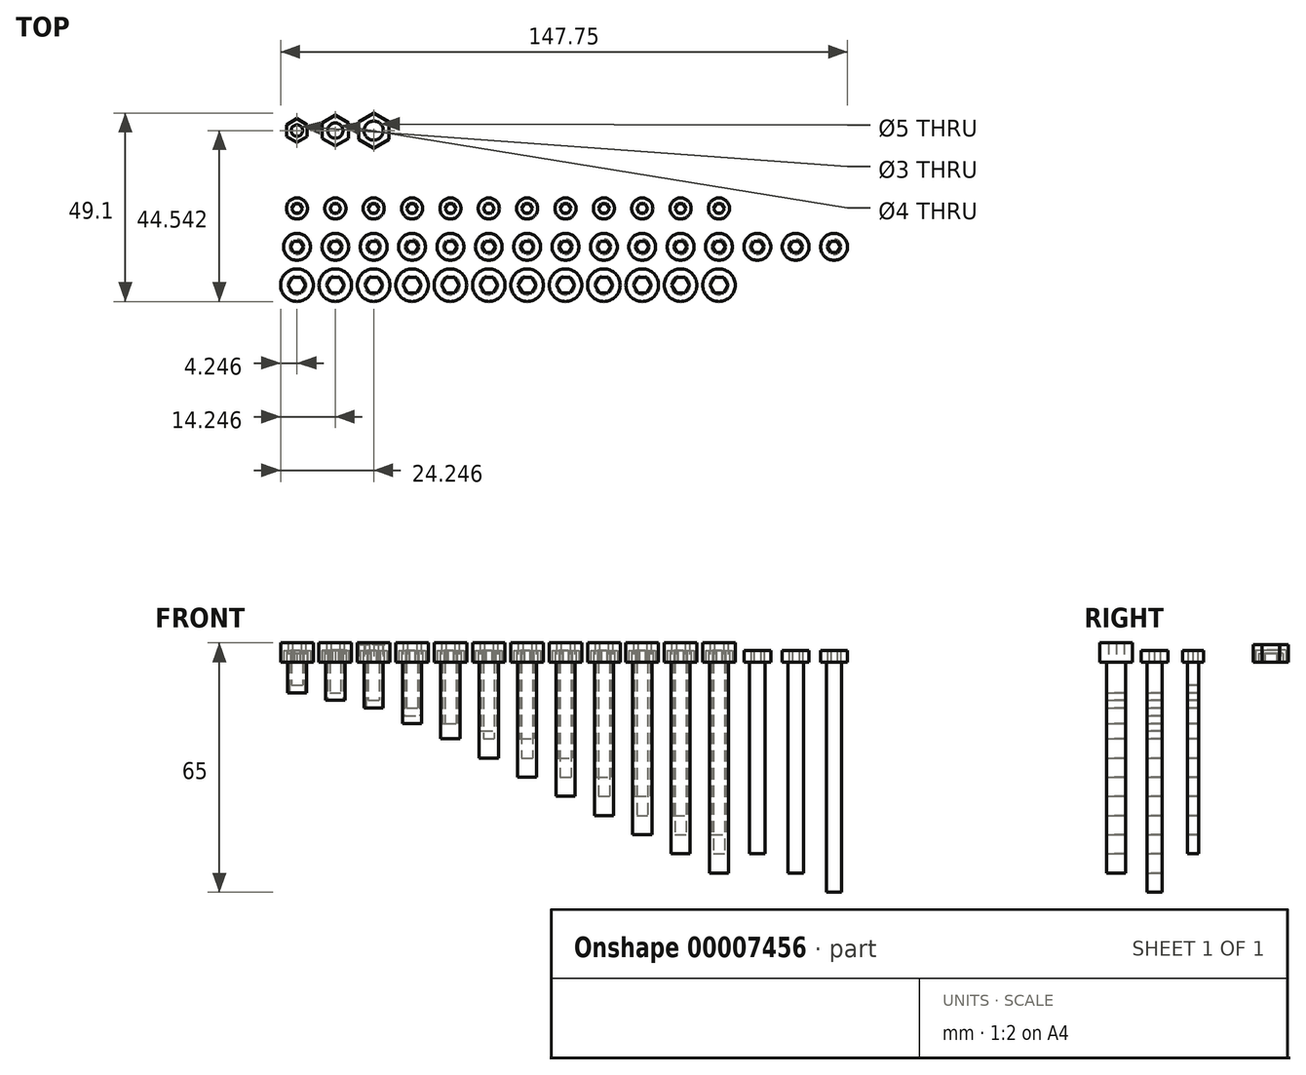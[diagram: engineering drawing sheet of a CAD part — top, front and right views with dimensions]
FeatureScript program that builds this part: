
annotation { "Feature Type Name" : "Feature", "Feature Type Description" : "" }
export const myFeature = defineFeature(function(context is Context, id is Id, definition is map)
    precondition{}
    {
        {
            var Q0;
            Q0=qCreatedBy(makeId("Top.planeOp"),FACE);
            var sketch = newSketch(context, id + "F0", { "sketchPlane" : qUnion([Q0])});
            skCircle(sketch, "E0", {"center": v(10, 10.3) * mm, "radius": 1.5 * mm});
            skLineSegment(sketch, "E1", {"start": v(0, 0) * mm, "end": v(0, 10) * mm, "construction": true});
            skLineSegment(sketch, "E2", {"start": v(0, 10) * mm, "end": v(10, 10.3) * mm, "construction": true});
            skLineSegment(sketch, "E3", {"start": v(10, 10.3) * mm, "end": v(20, 10.3) * mm, "construction": true});
            skLineSegment(sketch, "E4", {"start": v(20, 10.3) * mm, "end": v(30, 10.3) * mm, "construction": true});
            skLineSegment(sketch, "E5", {"start": v(30, 10.3) * mm, "end": v(40, 10.3) * mm, "construction": true});
            skCircle(sketch, "E6", {"center": v(20, 10.3) * mm, "radius": 2 * mm});
            skCircle(sketch, "E7", {"center": v(30, 10.3) * mm, "radius": 2.5 * mm});
            skCircle(sketch, "E8.cCircle", {"center": v(10, 10.3) * mm, "radius": 2.7 * mm, "construction": true});
            skLineSegment(sketch, "E8.0", {"start": v(12.7, 11.85) * mm, "end": v(12.7, 8.73) * mm});
            skLineSegment(sketch, "E8.1", {"start": v(12.7, 8.73) * mm, "end": v(10, 7.17) * mm});
            skLineSegment(sketch, "E8.2", {"start": v(10, 7.17) * mm, "end": v(7.3, 8.73) * mm});
            skLineSegment(sketch, "E8.3", {"start": v(7.3, 8.73) * mm, "end": v(7.3, 11.85) * mm});
            skLineSegment(sketch, "E8.4", {"start": v(7.3, 11.85) * mm, "end": v(10, 13.4) * mm});
            skLineSegment(sketch, "E8.5", {"start": v(10, 13.4) * mm, "end": v(12.7, 11.85) * mm});
            skPoint(sketch, "E8.0.midPoint", {"position": v(12.7, 10.3) * mm});
            skCircle(sketch, "E9.cCircle", {"center": v(20, 10.3) * mm, "radius": 3.45 * mm, "construction": true});
            skLineSegment(sketch, "E9.0", {"start": v(23.45, 12.28) * mm, "end": v(23.45, 8.3) * mm});
            skLineSegment(sketch, "E9.1", {"start": v(23.45, 8.3) * mm, "end": v(20, 6.3) * mm});
            skLineSegment(sketch, "E9.2", {"start": v(20, 6.3) * mm, "end": v(16.55, 8.3) * mm});
            skLineSegment(sketch, "E9.3", {"start": v(16.55, 8.3) * mm, "end": v(16.55, 12.28) * mm});
            skLineSegment(sketch, "E9.4", {"start": v(16.55, 12.28) * mm, "end": v(20, 14.28) * mm});
            skLineSegment(sketch, "E9.5", {"start": v(20, 14.28) * mm, "end": v(23.45, 12.28) * mm});
            skPoint(sketch, "E9.0.midPoint", {"position": v(23.45, 10.3) * mm});
            skCircle(sketch, "E10.cCircle", {"center": v(30, 10.3) * mm, "radius": 3.95 * mm, "construction": true});
            skLineSegment(sketch, "E10.0", {"start": v(33.95, 12.57) * mm, "end": v(33.95, 8.01) * mm});
            skLineSegment(sketch, "E10.1", {"start": v(33.95, 8.01) * mm, "end": v(30, 5.73) * mm});
            skLineSegment(sketch, "E10.2", {"start": v(30, 5.73) * mm, "end": v(26.05, 8.01) * mm});
            skLineSegment(sketch, "E10.3", {"start": v(26.05, 8.01) * mm, "end": v(26.05, 12.57) * mm});
            skLineSegment(sketch, "E10.4", {"start": v(26.05, 12.57) * mm, "end": v(30, 14.85) * mm});
            skLineSegment(sketch, "E10.5", {"start": v(30, 14.85) * mm, "end": v(33.95, 12.57) * mm});
            skPoint(sketch, "E10.0.midPoint", {"position": v(33.95, 10.3) * mm});
            skSolve(sketch);
        }
        {
            var Q0;
            Q0=makeQuery(id+"F0.imprint","IMPRINT",FACE,{"disambiguationData":[TD([[makeQuery(id+"F0.imprint","IMPRINT",EDGE,{"derivedFrom":sQuery(id+"F0.wireOp",EDGE,"E0")}),-1.0]])]});
            extrude(context, id + "F1", {"entities" : qUnion([Q0]), "depth" : 2.3 * mm});
        }
        {
            var Q0;
            Q0=makeQuery(id+"F0.imprint","IMPRINT",FACE,{"disambiguationData":[TD([[makeQuery(id+"F0.imprint","IMPRINT",EDGE,{"derivedFrom":sQuery(id+"F0.wireOp",EDGE,"E6")}),-1.0]])]});
            extrude(context, id + "F2", {"entities" : qUnion([Q0]), "depth" : 3.1 * mm});
        }
        {
            var Q0;
            Q0=makeQuery(id+"F0.imprint","IMPRINT",FACE,{"disambiguationData":[TD([[makeQuery(id+"F0.imprint","IMPRINT",EDGE,{"derivedFrom":sQuery(id+"F0.wireOp",EDGE,"E7")}),-1.0]])]});
            extrude(context, id + "F3", {"entities" : qUnion([Q0]), "depth" : 4.5 * mm});
        }
        {
            var Q0;
            Q0=qCreatedBy(makeId("Front.planeOp"),FACE);
            cPlane(context, id + "F4", {"entities" : qUnion([Q0]), "cplaneType" : CPlaneType.OFFSET, "offset" : 10 * mm, "width" : 150 * mm, "height" : 150 * mm});
        }
        {
            var Q0;
            Q0=qCreatedBy(id+"F4.planeOp",FACE);
            var sketch = newSketch(context, id + "F5", { "sketchPlane" : qUnion([Q0])});
            skLineSegment(sketch, "E11", {"start": v(10, 0) * mm, "end": v(0, 0) * mm, "construction": true});
            skLineSegment(sketch, "E12", {"start": v(10, 0) * mm, "end": v(20, 0) * mm, "construction": true});
            skLineSegment(sketch, "E13", {"start": v(0, 0) * mm, "end": v(0, 3) * mm, "construction": true});
            skLineSegment(sketch, "E14", {"start": v(0, 3) * mm, "end": v(153.62, 3) * mm, "construction": true});
            skLineSegment(sketch, "E15", {"start": v(10, 0) * mm, "end": v(10, 3) * mm});
            skLineSegment(sketch, "E16", {"start": v(10, 3) * mm, "end": v(12.75, 3) * mm});
            skLineSegment(sketch, "E17", {"start": v(12.75, 3) * mm, "end": v(12.75, 0) * mm});
            skLineSegment(sketch, "E18", {"start": v(12.75, 0) * mm, "end": v(11.45, 0) * mm});
            skLineSegment(sketch, "E19", {"start": v(11.45, 0) * mm, "end": v(11.45, -6) * mm});
            skLineSegment(sketch, "E20", {"start": v(11.45, -6) * mm, "end": v(10, -6) * mm});
            skLineSegment(sketch, "E21", {"start": v(10, -6) * mm, "end": v(10, 0) * mm});
            skLineSegment(sketch, "E22.1.0.0", {"start": v(22.75, 0) * mm, "end": v(21.45, 0) * mm});
            skLineSegment(sketch, "E22.1.0.1", {"start": v(20, 0) * mm, "end": v(20, 3) * mm});
            skLineSegment(sketch, "E22.1.0.2", {"start": v(20, 3) * mm, "end": v(22.75, 3) * mm});
            skLineSegment(sketch, "E22.1.0.3", {"start": v(22.75, 3) * mm, "end": v(22.75, 0) * mm});
            skLineSegment(sketch, "E22.1.0.4", {"start": v(20, 0) * mm, "end": v(30, 0) * mm, "construction": true});
            skLineSegment(sketch, "E22.2.0.0", {"start": v(32.75, 0) * mm, "end": v(31.45, 0) * mm});
            skLineSegment(sketch, "E22.2.0.1", {"start": v(30, 0) * mm, "end": v(30, 3) * mm});
            skLineSegment(sketch, "E22.2.0.2", {"start": v(30, 3) * mm, "end": v(32.75, 3) * mm});
            skLineSegment(sketch, "E22.2.0.3", {"start": v(32.75, 3) * mm, "end": v(32.75, 0) * mm});
            skLineSegment(sketch, "E22.2.0.4", {"start": v(30, 0) * mm, "end": v(40, 0) * mm, "construction": true});
            skLineSegment(sketch, "E22.3.0.0", {"start": v(42.75, 0) * mm, "end": v(41.45, 0) * mm});
            skLineSegment(sketch, "E22.3.0.1", {"start": v(40, 0) * mm, "end": v(40, 3) * mm});
            skLineSegment(sketch, "E22.3.0.2", {"start": v(40, 3) * mm, "end": v(42.75, 3) * mm});
            skLineSegment(sketch, "E22.3.0.3", {"start": v(42.75, 3) * mm, "end": v(42.75, 0) * mm});
            skLineSegment(sketch, "E22.3.0.4", {"start": v(40, 0) * mm, "end": v(50, 0) * mm, "construction": true});
            skLineSegment(sketch, "E22.4.0.0", {"start": v(52.75, 0) * mm, "end": v(51.45, 0) * mm});
            skLineSegment(sketch, "E22.4.0.1", {"start": v(50, 0) * mm, "end": v(50, 3) * mm});
            skLineSegment(sketch, "E22.4.0.2", {"start": v(50, 3) * mm, "end": v(52.75, 3) * mm});
            skLineSegment(sketch, "E22.4.0.3", {"start": v(52.75, 3) * mm, "end": v(52.75, 0) * mm});
            skLineSegment(sketch, "E22.4.0.4", {"start": v(50, 0) * mm, "end": v(60, 0) * mm, "construction": true});
            skLineSegment(sketch, "E22.5.0.0", {"start": v(62.75, 0) * mm, "end": v(61.45, 0) * mm});
            skLineSegment(sketch, "E22.5.0.1", {"start": v(60, 0) * mm, "end": v(60, 3) * mm});
            skLineSegment(sketch, "E22.5.0.2", {"start": v(60, 3) * mm, "end": v(62.75, 3) * mm});
            skLineSegment(sketch, "E22.5.0.3", {"start": v(62.75, 3) * mm, "end": v(62.75, 0) * mm});
            skLineSegment(sketch, "E22.5.0.4", {"start": v(60, 0) * mm, "end": v(70, 0) * mm, "construction": true});
            skLineSegment(sketch, "E22.6.0.0", {"start": v(72.75, 0) * mm, "end": v(71.45, 0) * mm});
            skLineSegment(sketch, "E22.6.0.1", {"start": v(70, 0) * mm, "end": v(70, 3) * mm});
            skLineSegment(sketch, "E22.6.0.2", {"start": v(70, 3) * mm, "end": v(72.75, 3) * mm});
            skLineSegment(sketch, "E22.6.0.3", {"start": v(72.75, 3) * mm, "end": v(72.75, 0) * mm});
            skLineSegment(sketch, "E22.6.0.4", {"start": v(70, 0) * mm, "end": v(80, 0) * mm, "construction": true});
            skLineSegment(sketch, "E22.7.0.0", {"start": v(82.75, 0) * mm, "end": v(81.45, 0) * mm});
            skLineSegment(sketch, "E22.7.0.1", {"start": v(80, 0) * mm, "end": v(80, 3) * mm});
            skLineSegment(sketch, "E22.7.0.2", {"start": v(80, 3) * mm, "end": v(82.75, 3) * mm});
            skLineSegment(sketch, "E22.7.0.3", {"start": v(82.75, 3) * mm, "end": v(82.75, 0) * mm});
            skLineSegment(sketch, "E22.7.0.4", {"start": v(80, 0) * mm, "end": v(90, 0) * mm, "construction": true});
            skLineSegment(sketch, "E22.8.0.0", {"start": v(92.75, 0) * mm, "end": v(91.45, 0) * mm});
            skLineSegment(sketch, "E22.8.0.1", {"start": v(90, 0) * mm, "end": v(90, 3) * mm});
            skLineSegment(sketch, "E22.8.0.2", {"start": v(90, 3) * mm, "end": v(92.75, 3) * mm});
            skLineSegment(sketch, "E22.8.0.3", {"start": v(92.75, 3) * mm, "end": v(92.75, 0) * mm});
            skLineSegment(sketch, "E22.8.0.4", {"start": v(90, 0) * mm, "end": v(100, 0) * mm, "construction": true});
            skLineSegment(sketch, "E22.9.0.0", {"start": v(102.75, 0) * mm, "end": v(101.45, 0) * mm});
            skLineSegment(sketch, "E22.9.0.1", {"start": v(100, 0) * mm, "end": v(100, 3) * mm});
            skLineSegment(sketch, "E22.9.0.2", {"start": v(100, 3) * mm, "end": v(102.75, 3) * mm});
            skLineSegment(sketch, "E22.9.0.3", {"start": v(102.75, 3) * mm, "end": v(102.75, 0) * mm});
            skLineSegment(sketch, "E22.9.0.4", {"start": v(100, 0) * mm, "end": v(110, 0) * mm, "construction": true});
            skLineSegment(sketch, "E22.direction1", {"start": v(11.45, 0) * mm, "end": v(21.45, 0) * mm, "construction": true});
            skLineSegment(sketch, "E23", {"start": v(21.45, 0) * mm, "end": v(21.45, -8) * mm});
            skLineSegment(sketch, "E24", {"start": v(21.45, -8) * mm, "end": v(20, -8) * mm});
            skLineSegment(sketch, "E25", {"start": v(20, -8) * mm, "end": v(20, 0) * mm});
            skLineSegment(sketch, "E26", {"start": v(30, 0) * mm, "end": v(30, -10) * mm});
            skLineSegment(sketch, "E27", {"start": v(30, -10) * mm, "end": v(31.45, -10) * mm});
            skLineSegment(sketch, "E28", {"start": v(31.45, -10) * mm, "end": v(31.45, 0) * mm});
            skLineSegment(sketch, "E29", {"start": v(40, 0) * mm, "end": v(40, -12) * mm});
            skLineSegment(sketch, "E30", {"start": v(40, -12) * mm, "end": v(41.45, -12) * mm});
            skLineSegment(sketch, "E31", {"start": v(41.45, -12) * mm, "end": v(41.45, 0) * mm});
            skLineSegment(sketch, "E32", {"start": v(50, 0) * mm, "end": v(50, -16) * mm});
            skLineSegment(sketch, "E33", {"start": v(50, -16) * mm, "end": v(51.45, -16) * mm});
            skLineSegment(sketch, "E34", {"start": v(51.45, -16) * mm, "end": v(51.45, 0) * mm});
            skLineSegment(sketch, "E35", {"start": v(60, 0) * mm, "end": v(60, -20) * mm});
            skLineSegment(sketch, "E36", {"start": v(60, -20) * mm, "end": v(61.45, -20) * mm});
            skLineSegment(sketch, "E37", {"start": v(61.45, -20) * mm, "end": v(61.45, 0) * mm});
            skLineSegment(sketch, "E38", {"start": v(70, 0) * mm, "end": v(70, -25) * mm});
            skLineSegment(sketch, "E39", {"start": v(70, -25) * mm, "end": v(71.45, -25) * mm});
            skLineSegment(sketch, "E40", {"start": v(71.45, -25) * mm, "end": v(71.45, 0) * mm});
            skLineSegment(sketch, "E41", {"start": v(80, 0) * mm, "end": v(80, -30) * mm});
            skLineSegment(sketch, "E42", {"start": v(80, -30) * mm, "end": v(81.45, -30) * mm});
            skLineSegment(sketch, "E43", {"start": v(81.45, -30) * mm, "end": v(81.45, 0) * mm});
            skLineSegment(sketch, "E44", {"start": v(90, 0) * mm, "end": v(90, -35) * mm});
            skLineSegment(sketch, "E45", {"start": v(90, -35) * mm, "end": v(91.45, -35) * mm});
            skLineSegment(sketch, "E46", {"start": v(91.45, -35) * mm, "end": v(91.45, 0) * mm});
            skLineSegment(sketch, "E47", {"start": v(100, 0) * mm, "end": v(100, -40) * mm});
            skLineSegment(sketch, "E48", {"start": v(100, -40) * mm, "end": v(101.45, -40) * mm});
            skLineSegment(sketch, "E49", {"start": v(101.45, -40) * mm, "end": v(101.45, 0) * mm});
            skLineSegment(sketch, "E50.0.10.0", {"start": v(112.75, 0) * mm, "end": v(111.45, 0) * mm});
            skLineSegment(sketch, "E50.3.10.0", {"start": v(110, 0) * mm, "end": v(110, 3) * mm});
            skLineSegment(sketch, "E50.6.10.0", {"start": v(110, 3) * mm, "end": v(112.75, 3) * mm});
            skLineSegment(sketch, "E50.9.10.0", {"start": v(112.75, 3) * mm, "end": v(112.75, 0) * mm});
            skLineSegment(sketch, "E50.12.10.0", {"start": v(110, 0) * mm, "end": v(120, 0) * mm, "construction": true});
            skLineSegment(sketch, "E50.0.11.0", {"start": v(122.75, 0) * mm, "end": v(121.45, 0) * mm});
            skLineSegment(sketch, "E50.3.11.0", {"start": v(120, 0) * mm, "end": v(120, 3) * mm});
            skLineSegment(sketch, "E50.6.11.0", {"start": v(120, 3) * mm, "end": v(122.75, 3) * mm});
            skLineSegment(sketch, "E50.9.11.0", {"start": v(122.75, 3) * mm, "end": v(122.75, 0) * mm});
            skLineSegment(sketch, "E50.12.11.0", {"start": v(120, 0) * mm, "end": v(130, 0) * mm, "construction": true});
            skLineSegment(sketch, "E51", {"start": v(110, 0) * mm, "end": v(110, -45) * mm});
            skLineSegment(sketch, "E52", {"start": v(110, -45) * mm, "end": v(111.45, -45) * mm});
            skLineSegment(sketch, "E53", {"start": v(111.45, -45) * mm, "end": v(111.45, 0) * mm});
            skLineSegment(sketch, "E54", {"start": v(120, 0) * mm, "end": v(120, -50) * mm});
            skLineSegment(sketch, "E55", {"start": v(120, -50) * mm, "end": v(121.45, -50) * mm});
            skLineSegment(sketch, "E56", {"start": v(121.45, -50) * mm, "end": v(121.45, 0) * mm});
            skSolve(sketch);
        }
        {
            var Q0;
            Q0=makeQuery(id+"F5.imprint","IMPRINT",FACE,{"disambiguationData":[TD([[makeQuery(id+"F5.imprint","IMPRINT",EDGE,{"derivedFrom":sQuery(id+"F5.wireOp",EDGE,"E15")}),-1.0]])]});
            var Q1;
            Q1=sQuery(id+"F5.wireOp",EDGE,"E15");
            revolve(context, id + "F6", {"entities" : qUnion([Q0]), "axis" : qUnion([Q1]), "revolveType" : RevolveType.FULL});
        }
        {
            var Q0;
            Q0=makeQuery(id+"F5.imprint","IMPRINT",FACE,{"disambiguationData":[TD([[makeQuery(id+"F5.imprint","IMPRINT",EDGE,{"derivedFrom":sQuery(id+"F5.wireOp",EDGE,"E22.1.0.0")}),-1.0]])]});
            var Q1;
            Q1=sQuery(id+"F5.wireOp",EDGE,"E22.1.0.1");
            revolve(context, id + "F7", {"entities" : qUnion([Q0]), "axis" : qUnion([Q1]), "revolveType" : RevolveType.FULL});
        }
        {
            var Q0;
            Q0=makeQuery(id+"F5.imprint","IMPRINT",FACE,{"disambiguationData":[TD([[makeQuery(id+"F5.imprint","IMPRINT",EDGE,{"derivedFrom":sQuery(id+"F5.wireOp",EDGE,"E22.2.0.0")}),-1.0]])]});
            var Q1;
            Q1=sQuery(id+"F5.wireOp",EDGE,"E22.2.0.1");
            revolve(context, id + "F8", {"entities" : qUnion([Q0]), "axis" : qUnion([Q1]), "revolveType" : RevolveType.FULL});
        }
        {
            var Q0;
            Q0=makeQuery(id+"F5.imprint","IMPRINT",FACE,{"disambiguationData":[TD([[makeQuery(id+"F5.imprint","IMPRINT",EDGE,{"derivedFrom":sQuery(id+"F5.wireOp",EDGE,"E22.3.0.0")}),-1.0]])]});
            var Q1;
            Q1=sQuery(id+"F5.wireOp",EDGE,"E22.3.0.1");
            revolve(context, id + "F9", {"entities" : qUnion([Q0]), "axis" : qUnion([Q1]), "revolveType" : RevolveType.FULL});
        }
        {
            var Q0;
            Q0=makeQuery(id+"F5.imprint","IMPRINT",FACE,{"disambiguationData":[TD([[makeQuery(id+"F5.imprint","IMPRINT",EDGE,{"derivedFrom":sQuery(id+"F5.wireOp",EDGE,"E22.4.0.0")}),-1.0]])]});
            var Q1;
            Q1=sQuery(id+"F5.wireOp",EDGE,"E22.4.0.1");
            revolve(context, id + "F10", {"entities" : qUnion([Q0]), "axis" : qUnion([Q1]), "revolveType" : RevolveType.FULL});
        }
        {
            var Q0;
            Q0=makeQuery(id+"F5.imprint","IMPRINT",FACE,{"disambiguationData":[TD([[makeQuery(id+"F5.imprint","IMPRINT",EDGE,{"derivedFrom":sQuery(id+"F5.wireOp",EDGE,"E22.5.0.0")}),-1.0]])]});
            var Q1;
            Q1=sQuery(id+"F5.wireOp",EDGE,"E22.5.0.1");
            revolve(context, id + "F11", {"entities" : qUnion([Q0]), "axis" : qUnion([Q1]), "revolveType" : RevolveType.FULL});
        }
        {
            var Q0;
            Q0=makeQuery(id+"F5.imprint","IMPRINT",FACE,{"disambiguationData":[TD([[makeQuery(id+"F5.imprint","IMPRINT",EDGE,{"derivedFrom":sQuery(id+"F5.wireOp",EDGE,"E22.6.0.0")}),-1.0]])]});
            var Q1;
            Q1=sQuery(id+"F5.wireOp",EDGE,"E22.6.0.1");
            revolve(context, id + "F12", {"entities" : qUnion([Q0]), "axis" : qUnion([Q1]), "revolveType" : RevolveType.FULL});
        }
        {
            var Q0;
            Q0=makeQuery(id+"F5.imprint","IMPRINT",FACE,{"disambiguationData":[TD([[makeQuery(id+"F5.imprint","IMPRINT",EDGE,{"derivedFrom":sQuery(id+"F5.wireOp",EDGE,"E22.7.0.0")}),-1.0]])]});
            var Q1;
            Q1=sQuery(id+"F5.wireOp",EDGE,"E22.7.0.1");
            revolve(context, id + "F13", {"entities" : qUnion([Q0]), "axis" : qUnion([Q1]), "revolveType" : RevolveType.FULL});
        }
        {
            var Q0;
            Q0=makeQuery(id+"F5.imprint","IMPRINT",FACE,{"disambiguationData":[TD([[makeQuery(id+"F5.imprint","IMPRINT",EDGE,{"derivedFrom":sQuery(id+"F5.wireOp",EDGE,"E22.8.0.0")}),-1.0]])]});
            var Q1;
            Q1=sQuery(id+"F5.wireOp",EDGE,"E22.8.0.1");
            revolve(context, id + "F14", {"entities" : qUnion([Q0]), "axis" : qUnion([Q1]), "revolveType" : RevolveType.FULL});
        }
        {
            var Q0;
            Q0=makeQuery(id+"F5.imprint","IMPRINT",FACE,{"disambiguationData":[TD([[makeQuery(id+"F5.imprint","IMPRINT",EDGE,{"derivedFrom":sQuery(id+"F5.wireOp",EDGE,"E22.9.0.0")}),-1.0]])]});
            var Q1;
            Q1=sQuery(id+"F5.wireOp",EDGE,"E22.9.0.1");
            revolve(context, id + "F15", {"entities" : qUnion([Q0]), "axis" : qUnion([Q1]), "revolveType" : RevolveType.FULL});
        }
        {
            var Q0;
            Q0=makeQuery(id+"F5.imprint","IMPRINT",FACE,{"disambiguationData":[TD([[makeQuery(id+"F5.imprint","IMPRINT",EDGE,{"derivedFrom":sQuery(id+"F5.wireOp",EDGE,"E50.0.10.0")}),-1.0]])]});
            var Q1;
            Q1=sQuery(id+"F5.wireOp",EDGE,"E50.3.10.0");
            revolve(context, id + "F16", {"entities" : qUnion([Q0]), "axis" : qUnion([Q1]), "revolveType" : RevolveType.FULL});
        }
        {
            var Q0;
            Q0=makeQuery(id+"F5.imprint","IMPRINT",FACE,{"disambiguationData":[TD([[makeQuery(id+"F5.imprint","IMPRINT",EDGE,{"derivedFrom":sQuery(id+"F5.wireOp",EDGE,"E50.0.11.0")}),-1.0]])]});
            var Q1;
            Q1=sQuery(id+"F5.wireOp",EDGE,"E50.3.11.0");
            revolve(context, id + "F17", {"entities" : qUnion([Q0]), "axis" : qUnion([Q1]), "revolveType" : RevolveType.FULL});
        }
        {
            var Q0;
            Q0=qCreatedBy(makeId("Front.planeOp"),FACE);
            cPlane(context, id + "F18", {"entities" : qUnion([Q0]), "cplaneType" : CPlaneType.OFFSET, "offset" : 20 * mm, "width" : 150 * mm, "height" : 150 * mm});
        }
        {
            var Q0;
            Q0=qCreatedBy(id+"F18.planeOp",FACE);
            var sketch = newSketch(context, id + "F19", { "sketchPlane" : qUnion([Q0])});
            skLineSegment(sketch, "E57", {"start": v(0, 0) * mm, "end": v(10, 0) * mm, "construction": true});
            skLineSegment(sketch, "E58", {"start": v(10, 0) * mm, "end": v(10, 3) * mm});
            skLineSegment(sketch, "E59", {"start": v(10, 3) * mm, "end": v(13.5, 3) * mm});
            skLineSegment(sketch, "E60", {"start": v(13.5, 3) * mm, "end": v(13.5, 0) * mm});
            skLineSegment(sketch, "E61", {"start": v(13.5, 0) * mm, "end": v(12, 0) * mm});
            skLineSegment(sketch, "E62.1.0.0", {"start": v(23.5, 0) * mm, "end": v(22, 0) * mm});
            skLineSegment(sketch, "E62.1.0.1", {"start": v(23.5, 3) * mm, "end": v(23.5, 0) * mm});
            skLineSegment(sketch, "E62.1.0.2", {"start": v(20, 0) * mm, "end": v(20, 3) * mm});
            skLineSegment(sketch, "E62.1.0.3", {"start": v(20, 3) * mm, "end": v(23.5, 3) * mm});
            skLineSegment(sketch, "E62.2.0.0", {"start": v(33.5, 0) * mm, "end": v(32, 0) * mm});
            skLineSegment(sketch, "E62.2.0.1", {"start": v(33.5, 3) * mm, "end": v(33.5, 0) * mm});
            skLineSegment(sketch, "E62.2.0.2", {"start": v(30, 0) * mm, "end": v(30, 3) * mm});
            skLineSegment(sketch, "E62.2.0.3", {"start": v(30, 3) * mm, "end": v(33.5, 3) * mm});
            skLineSegment(sketch, "E62.3.0.0", {"start": v(43.5, 0) * mm, "end": v(42, 0) * mm});
            skLineSegment(sketch, "E62.3.0.1", {"start": v(43.5, 3) * mm, "end": v(43.5, 0) * mm});
            skLineSegment(sketch, "E62.3.0.2", {"start": v(40, 0) * mm, "end": v(40, 3) * mm});
            skLineSegment(sketch, "E62.3.0.3", {"start": v(40, 3) * mm, "end": v(43.5, 3) * mm});
            skLineSegment(sketch, "E62.4.0.0", {"start": v(53.5, 0) * mm, "end": v(52, 0) * mm});
            skLineSegment(sketch, "E62.4.0.1", {"start": v(53.5, 3) * mm, "end": v(53.5, 0) * mm});
            skLineSegment(sketch, "E62.4.0.2", {"start": v(50, 0) * mm, "end": v(50, 3) * mm});
            skLineSegment(sketch, "E62.4.0.3", {"start": v(50, 3) * mm, "end": v(53.5, 3) * mm});
            skLineSegment(sketch, "E62.5.0.0", {"start": v(63.5, 0) * mm, "end": v(62, 0) * mm});
            skLineSegment(sketch, "E62.5.0.1", {"start": v(63.5, 3) * mm, "end": v(63.5, 0) * mm});
            skLineSegment(sketch, "E62.5.0.2", {"start": v(60, 0) * mm, "end": v(60, 3) * mm});
            skLineSegment(sketch, "E62.5.0.3", {"start": v(60, 3) * mm, "end": v(63.5, 3) * mm});
            skLineSegment(sketch, "E62.6.0.0", {"start": v(73.5, 0) * mm, "end": v(72, 0) * mm});
            skLineSegment(sketch, "E62.6.0.1", {"start": v(73.5, 3) * mm, "end": v(73.5, 0) * mm});
            skLineSegment(sketch, "E62.6.0.2", {"start": v(70, 0) * mm, "end": v(70, 3) * mm});
            skLineSegment(sketch, "E62.6.0.3", {"start": v(70, 3) * mm, "end": v(73.5, 3) * mm});
            skLineSegment(sketch, "E62.7.0.0", {"start": v(83.5, 0) * mm, "end": v(82, 0) * mm});
            skLineSegment(sketch, "E62.7.0.1", {"start": v(83.5, 3) * mm, "end": v(83.5, 0) * mm});
            skLineSegment(sketch, "E62.7.0.2", {"start": v(80, 0) * mm, "end": v(80, 3) * mm});
            skLineSegment(sketch, "E62.7.0.3", {"start": v(80, 3) * mm, "end": v(83.5, 3) * mm});
            skLineSegment(sketch, "E62.8.0.0", {"start": v(93.5, 0) * mm, "end": v(92, 0) * mm});
            skLineSegment(sketch, "E62.8.0.1", {"start": v(93.5, 3) * mm, "end": v(93.5, 0) * mm});
            skLineSegment(sketch, "E62.8.0.2", {"start": v(90, 0) * mm, "end": v(90, 3) * mm});
            skLineSegment(sketch, "E62.8.0.3", {"start": v(90, 3) * mm, "end": v(93.5, 3) * mm});
            skLineSegment(sketch, "E62.9.0.0", {"start": v(103.5, 0) * mm, "end": v(102, 0) * mm});
            skLineSegment(sketch, "E62.9.0.1", {"start": v(103.5, 3) * mm, "end": v(103.5, 0) * mm});
            skLineSegment(sketch, "E62.9.0.2", {"start": v(100, 0) * mm, "end": v(100, 3) * mm});
            skLineSegment(sketch, "E62.9.0.3", {"start": v(100, 3) * mm, "end": v(103.5, 3) * mm});
            skLineSegment(sketch, "E62.10.0.0", {"start": v(113.5, 0) * mm, "end": v(112, 0) * mm});
            skLineSegment(sketch, "E62.10.0.1", {"start": v(113.5, 3) * mm, "end": v(113.5, 0) * mm});
            skLineSegment(sketch, "E62.10.0.2", {"start": v(110, 0) * mm, "end": v(110, 3) * mm});
            skLineSegment(sketch, "E62.10.0.3", {"start": v(110, 3) * mm, "end": v(113.5, 3) * mm});
            skLineSegment(sketch, "E62.11.0.0", {"start": v(123.5, 0) * mm, "end": v(122, 0) * mm});
            skLineSegment(sketch, "E62.11.0.1", {"start": v(123.5, 3) * mm, "end": v(123.5, 0) * mm});
            skLineSegment(sketch, "E62.11.0.2", {"start": v(120, 0) * mm, "end": v(120, 3) * mm});
            skLineSegment(sketch, "E62.11.0.3", {"start": v(120, 3) * mm, "end": v(123.5, 3) * mm});
            skLineSegment(sketch, "E62.direction1", {"start": v(12, 0) * mm, "end": v(22, 0) * mm, "construction": true});
            skLineSegment(sketch, "E63", {"start": v(10, 0) * mm, "end": v(10, -8) * mm});
            skLineSegment(sketch, "E64", {"start": v(10, -8) * mm, "end": v(12, -8) * mm});
            skLineSegment(sketch, "E65", {"start": v(12, -8) * mm, "end": v(12, 0) * mm});
            skLineSegment(sketch, "E66", {"start": v(20, 0) * mm, "end": v(20, -10) * mm});
            skLineSegment(sketch, "E67", {"start": v(20, -10) * mm, "end": v(22, -10) * mm});
            skLineSegment(sketch, "E68", {"start": v(22, -10) * mm, "end": v(22, 0) * mm});
            skLineSegment(sketch, "E69", {"start": v(30, 0) * mm, "end": v(30, -12) * mm});
            skLineSegment(sketch, "E70", {"start": v(30, -12) * mm, "end": v(32, -12) * mm});
            skLineSegment(sketch, "E71", {"start": v(32, -12) * mm, "end": v(32, 0) * mm});
            skLineSegment(sketch, "E72", {"start": v(40, 0) * mm, "end": v(40, -14) * mm});
            skLineSegment(sketch, "E73", {"start": v(40, -14) * mm, "end": v(42, -14) * mm});
            skLineSegment(sketch, "E74", {"start": v(42, -14) * mm, "end": v(42, 0) * mm});
            skLineSegment(sketch, "E75", {"start": v(50, 0) * mm, "end": v(50, -16) * mm});
            skLineSegment(sketch, "E76", {"start": v(50, -16) * mm, "end": v(52, -16) * mm});
            skLineSegment(sketch, "E77", {"start": v(52, -16) * mm, "end": v(52, 0) * mm});
            skLineSegment(sketch, "E78", {"start": v(60, 0) * mm, "end": v(60, -18) * mm});
            skLineSegment(sketch, "E79", {"start": v(60, -18) * mm, "end": v(62, -18) * mm});
            skLineSegment(sketch, "E80", {"start": v(62, -18) * mm, "end": v(62, 0) * mm});
            skLineSegment(sketch, "E81", {"start": v(70, 0) * mm, "end": v(70, -20) * mm});
            skLineSegment(sketch, "E82", {"start": v(70, -20) * mm, "end": v(72, -20) * mm});
            skLineSegment(sketch, "E83", {"start": v(72, -20) * mm, "end": v(72, 0) * mm});
            skLineSegment(sketch, "E84", {"start": v(80, 0) * mm, "end": v(80, -25) * mm});
            skLineSegment(sketch, "E85", {"start": v(80, -25) * mm, "end": v(82, -25) * mm});
            skLineSegment(sketch, "E86", {"start": v(82, -25) * mm, "end": v(82, 0) * mm});
            skLineSegment(sketch, "E87", {"start": v(90, 0) * mm, "end": v(90, -30) * mm});
            skLineSegment(sketch, "E88", {"start": v(90, -30) * mm, "end": v(92, -30) * mm});
            skLineSegment(sketch, "E89", {"start": v(92, -30) * mm, "end": v(92, 0) * mm});
            skLineSegment(sketch, "E90", {"start": v(100, 0) * mm, "end": v(100, -35) * mm});
            skLineSegment(sketch, "E91", {"start": v(100, -35) * mm, "end": v(102, -35) * mm});
            skLineSegment(sketch, "E92", {"start": v(102, -35) * mm, "end": v(102, 0) * mm});
            skLineSegment(sketch, "E93", {"start": v(110, 0) * mm, "end": v(110, -40) * mm});
            skLineSegment(sketch, "E94", {"start": v(110, -40) * mm, "end": v(112, -40) * mm});
            skLineSegment(sketch, "E95", {"start": v(112, -40) * mm, "end": v(112, 0) * mm});
            skLineSegment(sketch, "E96", {"start": v(120, 0) * mm, "end": v(120, -45) * mm});
            skLineSegment(sketch, "E97", {"start": v(120, -45) * mm, "end": v(122, -45) * mm});
            skLineSegment(sketch, "E98", {"start": v(122, -45) * mm, "end": v(122, 0) * mm});
            skLineSegment(sketch, "E99.0.12.0", {"start": v(133.5, 0) * mm, "end": v(132, 0) * mm});
            skLineSegment(sketch, "E99.3.12.0", {"start": v(133.5, 3) * mm, "end": v(133.5, 0) * mm});
            skLineSegment(sketch, "E99.6.12.0", {"start": v(130, 0) * mm, "end": v(130, 3) * mm});
            skLineSegment(sketch, "E99.9.12.0", {"start": v(130, 3) * mm, "end": v(133.5, 3) * mm});
            skLineSegment(sketch, "E100", {"start": v(130, 0) * mm, "end": v(130, -50) * mm});
            skLineSegment(sketch, "E101", {"start": v(130, -50) * mm, "end": v(132, -50) * mm});
            skLineSegment(sketch, "E102", {"start": v(132, -50) * mm, "end": v(132, 0) * mm});
            skLineSegment(sketch, "E103.0.13.0", {"start": v(143.5, 0) * mm, "end": v(142, 0) * mm});
            skLineSegment(sketch, "E103.3.13.0", {"start": v(143.5, 3) * mm, "end": v(143.5, 0) * mm});
            skLineSegment(sketch, "E103.6.13.0", {"start": v(140, 0) * mm, "end": v(140, 3) * mm});
            skLineSegment(sketch, "E103.9.13.0", {"start": v(140, 3) * mm, "end": v(143.5, 3) * mm});
            skLineSegment(sketch, "E103.0.14.0", {"start": v(153.5, 0) * mm, "end": v(152, 0) * mm});
            skLineSegment(sketch, "E103.3.14.0", {"start": v(153.5, 3) * mm, "end": v(153.5, 0) * mm});
            skLineSegment(sketch, "E103.6.14.0", {"start": v(150, 0) * mm, "end": v(150, 3) * mm});
            skLineSegment(sketch, "E103.9.14.0", {"start": v(150, 3) * mm, "end": v(153.5, 3) * mm});
            skLineSegment(sketch, "E104", {"start": v(140, 0) * mm, "end": v(140, -55) * mm});
            skLineSegment(sketch, "E105", {"start": v(140, -55) * mm, "end": v(142, -55) * mm});
            skLineSegment(sketch, "E106", {"start": v(142, -55) * mm, "end": v(142, 0) * mm});
            skLineSegment(sketch, "E107", {"start": v(150, 0) * mm, "end": v(150, -60) * mm});
            skLineSegment(sketch, "E108", {"start": v(150, -60) * mm, "end": v(152, -60) * mm});
            skLineSegment(sketch, "E109", {"start": v(152, -60) * mm, "end": v(152, 0) * mm});
            skSolve(sketch);
        }
        {
            var Q0;
            Q0=makeQuery(id+"F19.imprint","IMPRINT",FACE,{"disambiguationData":[TD([[makeQuery(id+"F19.imprint","IMPRINT",EDGE,{"derivedFrom":sQuery(id+"F19.wireOp",EDGE,"E58")}),-1.0]])]});
            var Q1;
            Q1=sQuery(id+"F19.wireOp",EDGE,"E58");
            revolve(context, id + "F20", {"entities" : qUnion([Q0]), "axis" : qUnion([Q1]), "revolveType" : RevolveType.FULL});
        }
        {
            var Q0;
            Q0=makeQuery(id+"F19.imprint","IMPRINT",FACE,{"disambiguationData":[TD([[makeQuery(id+"F19.imprint","IMPRINT",EDGE,{"derivedFrom":sQuery(id+"F19.wireOp",EDGE,"E62.1.0.0")}),-1.0]])]});
            var Q1;
            Q1=sQuery(id+"F19.wireOp",EDGE,"E62.1.0.2");
            revolve(context, id + "F21", {"entities" : qUnion([Q0]), "axis" : qUnion([Q1]), "revolveType" : RevolveType.FULL});
        }
        {
            var Q0;
            Q0=makeQuery(id+"F19.imprint","IMPRINT",FACE,{"disambiguationData":[TD([[makeQuery(id+"F19.imprint","IMPRINT",EDGE,{"derivedFrom":sQuery(id+"F19.wireOp",EDGE,"E62.2.0.0")}),-1.0]])]});
            var Q1;
            Q1=sQuery(id+"F19.wireOp",EDGE,"E62.2.0.2");
            revolve(context, id + "F22", {"entities" : qUnion([Q0]), "axis" : qUnion([Q1]), "revolveType" : RevolveType.FULL});
        }
        {
            var Q0;
            Q0=makeQuery(id+"F19.imprint","IMPRINT",FACE,{"disambiguationData":[TD([[makeQuery(id+"F19.imprint","IMPRINT",EDGE,{"derivedFrom":sQuery(id+"F19.wireOp",EDGE,"E62.3.0.0")}),-1.0]])]});
            var Q1;
            Q1=sQuery(id+"F19.wireOp",EDGE,"E62.3.0.2");
            revolve(context, id + "F23", {"entities" : qUnion([Q0]), "axis" : qUnion([Q1]), "revolveType" : RevolveType.FULL});
        }
        {
            var Q0;
            Q0=makeQuery(id+"F19.imprint","IMPRINT",FACE,{"disambiguationData":[TD([[makeQuery(id+"F19.imprint","IMPRINT",EDGE,{"derivedFrom":sQuery(id+"F19.wireOp",EDGE,"E62.4.0.0")}),-1.0]])]});
            var Q1;
            Q1=sQuery(id+"F19.wireOp",EDGE,"E62.4.0.2");
            revolve(context, id + "F24", {"entities" : qUnion([Q0]), "axis" : qUnion([Q1]), "revolveType" : RevolveType.FULL});
        }
        {
            var Q0;
            Q0=makeQuery(id+"F19.imprint","IMPRINT",FACE,{"disambiguationData":[TD([[makeQuery(id+"F19.imprint","IMPRINT",EDGE,{"derivedFrom":sQuery(id+"F19.wireOp",EDGE,"E62.5.0.0")}),-1.0]])]});
            var Q1;
            Q1=sQuery(id+"F19.wireOp",EDGE,"E62.5.0.2");
            revolve(context, id + "F25", {"entities" : qUnion([Q0]), "axis" : qUnion([Q1]), "revolveType" : RevolveType.FULL});
        }
        {
            var Q0;
            Q0=makeQuery(id+"F19.imprint","IMPRINT",FACE,{"disambiguationData":[TD([[makeQuery(id+"F19.imprint","IMPRINT",EDGE,{"derivedFrom":sQuery(id+"F19.wireOp",EDGE,"E62.6.0.0")}),-1.0]])]});
            var Q1;
            Q1=sQuery(id+"F19.wireOp",EDGE,"E62.6.0.2");
            revolve(context, id + "F26", {"entities" : qUnion([Q0]), "axis" : qUnion([Q1]), "revolveType" : RevolveType.FULL});
        }
        {
            var Q0;
            Q0=makeQuery(id+"F19.imprint","IMPRINT",FACE,{"disambiguationData":[TD([[makeQuery(id+"F19.imprint","IMPRINT",EDGE,{"derivedFrom":sQuery(id+"F19.wireOp",EDGE,"E62.7.0.0")}),-1.0]])]});
            var Q1;
            Q1=sQuery(id+"F19.wireOp",EDGE,"E62.7.0.2");
            revolve(context, id + "F27", {"entities" : qUnion([Q0]), "axis" : qUnion([Q1]), "revolveType" : RevolveType.FULL});
        }
        {
            var Q0;
            Q0=makeQuery(id+"F19.imprint","IMPRINT",FACE,{"disambiguationData":[TD([[makeQuery(id+"F19.imprint","IMPRINT",EDGE,{"derivedFrom":sQuery(id+"F19.wireOp",EDGE,"E62.8.0.0")}),-1.0]])]});
            var Q1;
            Q1=sQuery(id+"F19.wireOp",EDGE,"E62.8.0.2");
            revolve(context, id + "F28", {"entities" : qUnion([Q0]), "axis" : qUnion([Q1]), "revolveType" : RevolveType.FULL});
        }
        {
            var Q0;
            Q0=makeQuery(id+"F19.imprint","IMPRINT",FACE,{"disambiguationData":[TD([[makeQuery(id+"F19.imprint","IMPRINT",EDGE,{"derivedFrom":sQuery(id+"F19.wireOp",EDGE,"E62.9.0.0")}),-1.0]])]});
            var Q1;
            Q1=sQuery(id+"F19.wireOp",EDGE,"E62.9.0.2");
            revolve(context, id + "F29", {"entities" : qUnion([Q0]), "axis" : qUnion([Q1]), "revolveType" : RevolveType.FULL});
        }
        {
            var Q0;
            Q0=makeQuery(id+"F19.imprint","IMPRINT",FACE,{"disambiguationData":[TD([[makeQuery(id+"F19.imprint","IMPRINT",EDGE,{"derivedFrom":sQuery(id+"F19.wireOp",EDGE,"E62.10.0.0")}),-1.0]])]});
            var Q1;
            Q1=sQuery(id+"F19.wireOp",EDGE,"E62.10.0.2");
            revolve(context, id + "F30", {"entities" : qUnion([Q0]), "axis" : qUnion([Q1]), "revolveType" : RevolveType.FULL});
        }
        {
            var Q0;
            Q0=makeQuery(id+"F19.imprint","IMPRINT",FACE,{"disambiguationData":[TD([[makeQuery(id+"F19.imprint","IMPRINT",EDGE,{"derivedFrom":sQuery(id+"F19.wireOp",EDGE,"E62.11.0.0")}),-1.0]])]});
            var Q1;
            Q1=sQuery(id+"F19.wireOp",EDGE,"E62.11.0.2");
            revolve(context, id + "F31", {"entities" : qUnion([Q0]), "axis" : qUnion([Q1]), "revolveType" : RevolveType.FULL});
        }
        {
            var Q0;
            Q0=makeQuery(id+"F19.imprint","IMPRINT",FACE,{"disambiguationData":[TD([[makeQuery(id+"F19.imprint","IMPRINT",EDGE,{"derivedFrom":sQuery(id+"F19.wireOp",EDGE,"E99.0.12.0")}),-1.0]])]});
            var Q1;
            Q1=sQuery(id+"F19.wireOp",EDGE,"E99.6.12.0");
            revolve(context, id + "F32", {"entities" : qUnion([Q0]), "axis" : qUnion([Q1]), "revolveType" : RevolveType.FULL});
        }
        {
            var Q0;
            Q0=makeQuery(id+"F19.imprint","IMPRINT",FACE,{"disambiguationData":[TD([[makeQuery(id+"F19.imprint","IMPRINT",EDGE,{"derivedFrom":sQuery(id+"F19.wireOp",EDGE,"E103.0.13.0")}),-1.0]])]});
            var Q1;
            Q1=sQuery(id+"F19.wireOp",EDGE,"E103.6.13.0");
            revolve(context, id + "F33", {"entities" : qUnion([Q0]), "axis" : qUnion([Q1]), "revolveType" : RevolveType.FULL});
        }
        {
            var Q0;
            Q0=makeQuery(id+"F19.imprint","IMPRINT",FACE,{"disambiguationData":[TD([[makeQuery(id+"F19.imprint","IMPRINT",EDGE,{"derivedFrom":sQuery(id+"F19.wireOp",EDGE,"E103.0.14.0")}),-1.0]])]});
            var Q1;
            Q1=sQuery(id+"F19.wireOp",EDGE,"E103.6.14.0");
            revolve(context, id + "F34", {"entities" : qUnion([Q0]), "axis" : qUnion([Q1]), "revolveType" : RevolveType.FULL});
        }
        {
            var Q0;
            Q0=qCreatedBy(makeId("Front.planeOp"),FACE);
            cPlane(context, id + "F35", {"entities" : qUnion([Q0]), "cplaneType" : CPlaneType.OFFSET, "offset" : 30 * mm, "width" : 150 * mm, "height" : 150 * mm});
        }
        {
            var Q0;
            Q0=qCreatedBy(id+"F35.planeOp",FACE);
            var sketch = newSketch(context, id + "F36", { "sketchPlane" : qUnion([Q0])});
            skLineSegment(sketch, "E110", {"start": v(0, 0) * mm, "end": v(10, 0) * mm, "construction": true});
            skLineSegment(sketch, "E111", {"start": v(10, 0) * mm, "end": v(10, 5) * mm});
            skLineSegment(sketch, "E112", {"start": v(10, 5) * mm, "end": v(14.25, 5) * mm});
            skLineSegment(sketch, "E113", {"start": v(14.25, 5) * mm, "end": v(14.25, 0) * mm});
            skLineSegment(sketch, "E114", {"start": v(14.25, 0) * mm, "end": v(12.5, 0) * mm});
            skLineSegment(sketch, "E115", {"start": v(12.5, 0) * mm, "end": v(12.5, -8) * mm});
            skLineSegment(sketch, "E116", {"start": v(12.5, -8) * mm, "end": v(10, -8) * mm});
            skLineSegment(sketch, "E117", {"start": v(10, -8) * mm, "end": v(10, 0) * mm});
            skLineSegment(sketch, "E118", {"start": v(10, 0) * mm, "end": v(12.5, 0) * mm, "construction": true});
            skLineSegment(sketch, "E119.1.0.0", {"start": v(20, 0) * mm, "end": v(20, 5) * mm});
            skLineSegment(sketch, "E119.1.0.1", {"start": v(24.25, 5) * mm, "end": v(24.25, 0) * mm});
            skLineSegment(sketch, "E119.1.0.2", {"start": v(20, 5) * mm, "end": v(24.25, 5) * mm});
            skLineSegment(sketch, "E119.1.0.3", {"start": v(24.25, 0) * mm, "end": v(22.5, 0) * mm});
            skLineSegment(sketch, "E119.1.0.4", {"start": v(20, 0) * mm, "end": v(22.5, 0) * mm, "construction": true});
            skLineSegment(sketch, "E119.2.0.0", {"start": v(30, 0) * mm, "end": v(30, 5) * mm});
            skLineSegment(sketch, "E119.2.0.1", {"start": v(34.25, 5) * mm, "end": v(34.25, 0) * mm});
            skLineSegment(sketch, "E119.2.0.2", {"start": v(30, 5) * mm, "end": v(34.25, 5) * mm});
            skLineSegment(sketch, "E119.2.0.3", {"start": v(34.25, 0) * mm, "end": v(32.5, 0) * mm});
            skLineSegment(sketch, "E119.2.0.4", {"start": v(30, 0) * mm, "end": v(32.5, 0) * mm, "construction": true});
            skLineSegment(sketch, "E119.3.0.0", {"start": v(40, 0) * mm, "end": v(40, 5) * mm});
            skLineSegment(sketch, "E119.3.0.1", {"start": v(44.25, 5) * mm, "end": v(44.25, 0) * mm});
            skLineSegment(sketch, "E119.3.0.2", {"start": v(40, 5) * mm, "end": v(44.25, 5) * mm});
            skLineSegment(sketch, "E119.3.0.3", {"start": v(44.25, 0) * mm, "end": v(42.5, 0) * mm});
            skLineSegment(sketch, "E119.3.0.4", {"start": v(40, 0) * mm, "end": v(42.5, 0) * mm, "construction": true});
            skLineSegment(sketch, "E119.4.0.0", {"start": v(50, 0) * mm, "end": v(50, 5) * mm});
            skLineSegment(sketch, "E119.4.0.1", {"start": v(54.25, 5) * mm, "end": v(54.25, 0) * mm});
            skLineSegment(sketch, "E119.4.0.2", {"start": v(50, 5) * mm, "end": v(54.25, 5) * mm});
            skLineSegment(sketch, "E119.4.0.3", {"start": v(54.25, 0) * mm, "end": v(52.5, 0) * mm});
            skLineSegment(sketch, "E119.4.0.4", {"start": v(50, 0) * mm, "end": v(52.5, 0) * mm, "construction": true});
            skLineSegment(sketch, "E119.5.0.0", {"start": v(60, 0) * mm, "end": v(60, 5) * mm});
            skLineSegment(sketch, "E119.5.0.1", {"start": v(64.25, 5) * mm, "end": v(64.25, 0) * mm});
            skLineSegment(sketch, "E119.5.0.2", {"start": v(60, 5) * mm, "end": v(64.25, 5) * mm});
            skLineSegment(sketch, "E119.5.0.3", {"start": v(64.25, 0) * mm, "end": v(62.5, 0) * mm});
            skLineSegment(sketch, "E119.5.0.4", {"start": v(60, 0) * mm, "end": v(62.5, 0) * mm, "construction": true});
            skLineSegment(sketch, "E119.6.0.0", {"start": v(70, 0) * mm, "end": v(70, 5) * mm});
            skLineSegment(sketch, "E119.6.0.1", {"start": v(74.25, 5) * mm, "end": v(74.25, 0) * mm});
            skLineSegment(sketch, "E119.6.0.2", {"start": v(70, 5) * mm, "end": v(74.25, 5) * mm});
            skLineSegment(sketch, "E119.6.0.3", {"start": v(74.25, 0) * mm, "end": v(72.5, 0) * mm});
            skLineSegment(sketch, "E119.6.0.4", {"start": v(70, 0) * mm, "end": v(72.5, 0) * mm, "construction": true});
            skLineSegment(sketch, "E119.7.0.0", {"start": v(80, 0) * mm, "end": v(80, 5) * mm});
            skLineSegment(sketch, "E119.7.0.1", {"start": v(84.25, 5) * mm, "end": v(84.25, 0) * mm});
            skLineSegment(sketch, "E119.7.0.2", {"start": v(80, 5) * mm, "end": v(84.25, 5) * mm});
            skLineSegment(sketch, "E119.7.0.3", {"start": v(84.25, 0) * mm, "end": v(82.5, 0) * mm});
            skLineSegment(sketch, "E119.7.0.4", {"start": v(80, 0) * mm, "end": v(82.5, 0) * mm, "construction": true});
            skLineSegment(sketch, "E119.8.0.0", {"start": v(90, 0) * mm, "end": v(90, 5) * mm});
            skLineSegment(sketch, "E119.8.0.1", {"start": v(94.25, 5) * mm, "end": v(94.25, 0) * mm});
            skLineSegment(sketch, "E119.8.0.2", {"start": v(90, 5) * mm, "end": v(94.25, 5) * mm});
            skLineSegment(sketch, "E119.8.0.3", {"start": v(94.25, 0) * mm, "end": v(92.5, 0) * mm});
            skLineSegment(sketch, "E119.8.0.4", {"start": v(90, 0) * mm, "end": v(92.5, 0) * mm, "construction": true});
            skLineSegment(sketch, "E119.9.0.0", {"start": v(100, 0) * mm, "end": v(100, 5) * mm});
            skLineSegment(sketch, "E119.9.0.1", {"start": v(104.25, 5) * mm, "end": v(104.25, 0) * mm});
            skLineSegment(sketch, "E119.9.0.2", {"start": v(100, 5) * mm, "end": v(104.25, 5) * mm});
            skLineSegment(sketch, "E119.9.0.3", {"start": v(104.25, 0) * mm, "end": v(102.5, 0) * mm});
            skLineSegment(sketch, "E119.9.0.4", {"start": v(100, 0) * mm, "end": v(102.5, 0) * mm, "construction": true});
            skLineSegment(sketch, "E119.10.0.0", {"start": v(110, 0) * mm, "end": v(110, 5) * mm});
            skLineSegment(sketch, "E119.10.0.1", {"start": v(114.25, 5) * mm, "end": v(114.25, 0) * mm});
            skLineSegment(sketch, "E119.10.0.2", {"start": v(110, 5) * mm, "end": v(114.25, 5) * mm});
            skLineSegment(sketch, "E119.10.0.3", {"start": v(114.25, 0) * mm, "end": v(112.5, 0) * mm});
            skLineSegment(sketch, "E119.10.0.4", {"start": v(110, 0) * mm, "end": v(112.5, 0) * mm, "construction": true});
            skLineSegment(sketch, "E119.11.0.0", {"start": v(120, 0) * mm, "end": v(120, 5) * mm});
            skLineSegment(sketch, "E119.11.0.1", {"start": v(124.25, 5) * mm, "end": v(124.25, 0) * mm});
            skLineSegment(sketch, "E119.11.0.2", {"start": v(120, 5) * mm, "end": v(124.25, 5) * mm});
            skLineSegment(sketch, "E119.11.0.3", {"start": v(124.25, 0) * mm, "end": v(122.5, 0) * mm});
            skLineSegment(sketch, "E119.11.0.4", {"start": v(120, 0) * mm, "end": v(122.5, 0) * mm, "construction": true});
            skLineSegment(sketch, "E119.direction1", {"start": v(10, 0) * mm, "end": v(20, 0) * mm, "construction": true});
            skLineSegment(sketch, "E120", {"start": v(20, 0) * mm, "end": v(20, -10) * mm});
            skLineSegment(sketch, "E121", {"start": v(20, -10) * mm, "end": v(22.5, -10) * mm});
            skLineSegment(sketch, "E122", {"start": v(22.5, -10) * mm, "end": v(22.5, 0) * mm});
            skLineSegment(sketch, "E123", {"start": v(30, 0) * mm, "end": v(30, -12) * mm});
            skLineSegment(sketch, "E124", {"start": v(30, -12) * mm, "end": v(32.5, -12) * mm});
            skLineSegment(sketch, "E125", {"start": v(32.5, -12) * mm, "end": v(32.5, 0) * mm});
            skLineSegment(sketch, "E126", {"start": v(40, 0) * mm, "end": v(40, -16) * mm});
            skLineSegment(sketch, "E127", {"start": v(40, -16) * mm, "end": v(42.5, -16) * mm});
            skLineSegment(sketch, "E128", {"start": v(42.5, -16) * mm, "end": v(42.5, 0) * mm});
            skLineSegment(sketch, "E129", {"start": v(50, 0) * mm, "end": v(50, -20) * mm});
            skLineSegment(sketch, "E130", {"start": v(50, -20) * mm, "end": v(52.5, -20) * mm});
            skLineSegment(sketch, "E131", {"start": v(52.5, -20) * mm, "end": v(52.5, 0) * mm});
            skLineSegment(sketch, "E132", {"start": v(60, 0) * mm, "end": v(60, -25) * mm});
            skLineSegment(sketch, "E133", {"start": v(60, -25) * mm, "end": v(62.5, -25) * mm});
            skLineSegment(sketch, "E134", {"start": v(62.5, -25) * mm, "end": v(62.5, 0) * mm});
            skLineSegment(sketch, "E135", {"start": v(70, 0) * mm, "end": v(70, -30) * mm});
            skLineSegment(sketch, "E136", {"start": v(70, -30) * mm, "end": v(72.5, -30) * mm});
            skLineSegment(sketch, "E137", {"start": v(72.5, -30) * mm, "end": v(72.5, 0) * mm});
            skLineSegment(sketch, "E138", {"start": v(80, 0) * mm, "end": v(80, -35) * mm});
            skLineSegment(sketch, "E139", {"start": v(80, -35) * mm, "end": v(82.5, -35) * mm});
            skLineSegment(sketch, "E140", {"start": v(82.5, -35) * mm, "end": v(82.5, 0) * mm});
            skLineSegment(sketch, "E141", {"start": v(90, 0) * mm, "end": v(90, -40) * mm});
            skLineSegment(sketch, "E142", {"start": v(90, -40) * mm, "end": v(92.5, -40) * mm});
            skLineSegment(sketch, "E143", {"start": v(92.5, -40) * mm, "end": v(92.5, 0) * mm});
            skLineSegment(sketch, "E144", {"start": v(100, 0) * mm, "end": v(100, -45) * mm});
            skLineSegment(sketch, "E145", {"start": v(100, -45) * mm, "end": v(102.5, -45) * mm});
            skLineSegment(sketch, "E146", {"start": v(102.5, -45) * mm, "end": v(102.5, 0) * mm});
            skLineSegment(sketch, "E147", {"start": v(110, 0) * mm, "end": v(110, -50) * mm});
            skLineSegment(sketch, "E148", {"start": v(110, -50) * mm, "end": v(112.5, -50) * mm});
            skLineSegment(sketch, "E149", {"start": v(112.5, -50) * mm, "end": v(112.5, 0) * mm});
            skLineSegment(sketch, "E150", {"start": v(120, 0) * mm, "end": v(120, -55) * mm});
            skLineSegment(sketch, "E151", {"start": v(120, -55) * mm, "end": v(122.5, -55) * mm});
            skLineSegment(sketch, "E152", {"start": v(122.5, -55) * mm, "end": v(122.5, 0) * mm});
            skSolve(sketch);
        }
        {
            var Q0;
            Q0=makeQuery(id+"F36.imprint","IMPRINT",FACE,{"disambiguationData":[TD([[makeQuery(id+"F36.imprint","IMPRINT",EDGE,{"derivedFrom":sQuery(id+"F36.wireOp",EDGE,"E111")}),-1.0]])]});
            var Q1;
            Q1=sQuery(id+"F36.wireOp",EDGE,"E111");
            revolve(context, id + "F37", {"entities" : qUnion([Q0]), "axis" : qUnion([Q1]), "revolveType" : RevolveType.FULL});
        }
        {
            var Q0;
            Q0=makeQuery(id+"F36.imprint","IMPRINT",FACE,{"disambiguationData":[TD([[makeQuery(id+"F36.imprint","IMPRINT",EDGE,{"derivedFrom":sQuery(id+"F36.wireOp",EDGE,"E119.1.0.0")}),-1.0]])]});
            var Q1;
            Q1=sQuery(id+"F36.wireOp",EDGE,"E119.1.0.0");
            revolve(context, id + "F38", {"entities" : qUnion([Q0]), "axis" : qUnion([Q1]), "revolveType" : RevolveType.FULL});
        }
        {
            var Q0;
            Q0=makeQuery(id+"F36.imprint","IMPRINT",FACE,{"disambiguationData":[TD([[makeQuery(id+"F36.imprint","IMPRINT",EDGE,{"derivedFrom":sQuery(id+"F36.wireOp",EDGE,"E119.2.0.0")}),-1.0]])]});
            var Q1;
            Q1=sQuery(id+"F36.wireOp",EDGE,"E119.2.0.0");
            revolve(context, id + "F39", {"entities" : qUnion([Q0]), "axis" : qUnion([Q1]), "revolveType" : RevolveType.FULL});
        }
        {
            var Q0;
            Q0=makeQuery(id+"F36.imprint","IMPRINT",FACE,{"disambiguationData":[TD([[makeQuery(id+"F36.imprint","IMPRINT",EDGE,{"derivedFrom":sQuery(id+"F36.wireOp",EDGE,"E119.3.0.0")}),-1.0]])]});
            var Q1;
            Q1=sQuery(id+"F36.wireOp",EDGE,"E119.3.0.0");
            revolve(context, id + "F40", {"entities" : qUnion([Q0]), "axis" : qUnion([Q1]), "revolveType" : RevolveType.FULL});
        }
        {
            var Q0;
            Q0=makeQuery(id+"F36.imprint","IMPRINT",FACE,{"disambiguationData":[TD([[makeQuery(id+"F36.imprint","IMPRINT",EDGE,{"derivedFrom":sQuery(id+"F36.wireOp",EDGE,"E119.4.0.0")}),-1.0]])]});
            var Q1;
            Q1=sQuery(id+"F36.wireOp",EDGE,"E119.4.0.0");
            revolve(context, id + "F41", {"entities" : qUnion([Q0]), "axis" : qUnion([Q1]), "revolveType" : RevolveType.FULL});
        }
        {
            var Q0;
            Q0=makeQuery(id+"F36.imprint","IMPRINT",FACE,{"disambiguationData":[TD([[makeQuery(id+"F36.imprint","IMPRINT",EDGE,{"derivedFrom":sQuery(id+"F36.wireOp",EDGE,"E119.5.0.0")}),-1.0]])]});
            var Q1;
            Q1=sQuery(id+"F36.wireOp",EDGE,"E119.5.0.0");
            revolve(context, id + "F42", {"entities" : qUnion([Q0]), "axis" : qUnion([Q1]), "revolveType" : RevolveType.FULL});
        }
        {
            var Q0;
            Q0=makeQuery(id+"F36.imprint","IMPRINT",FACE,{"disambiguationData":[TD([[makeQuery(id+"F36.imprint","IMPRINT",EDGE,{"derivedFrom":sQuery(id+"F36.wireOp",EDGE,"E119.6.0.0")}),-1.0]])]});
            var Q1;
            Q1=sQuery(id+"F36.wireOp",EDGE,"E119.6.0.0");
            revolve(context, id + "F43", {"entities" : qUnion([Q0]), "axis" : qUnion([Q1]), "revolveType" : RevolveType.FULL});
        }
        {
            var Q0;
            Q0=makeQuery(id+"F36.imprint","IMPRINT",FACE,{"disambiguationData":[TD([[makeQuery(id+"F36.imprint","IMPRINT",EDGE,{"derivedFrom":sQuery(id+"F36.wireOp",EDGE,"E119.7.0.0")}),-1.0]])]});
            var Q1;
            Q1=sQuery(id+"F36.wireOp",EDGE,"E119.7.0.0");
            revolve(context, id + "F44", {"entities" : qUnion([Q0]), "axis" : qUnion([Q1]), "revolveType" : RevolveType.FULL});
        }
        {
            var Q0;
            Q0=makeQuery(id+"F36.imprint","IMPRINT",FACE,{"disambiguationData":[TD([[makeQuery(id+"F36.imprint","IMPRINT",EDGE,{"derivedFrom":sQuery(id+"F36.wireOp",EDGE,"E119.8.0.0")}),-1.0]])]});
            var Q1;
            Q1=sQuery(id+"F36.wireOp",EDGE,"E119.8.0.0");
            revolve(context, id + "F45", {"entities" : qUnion([Q0]), "axis" : qUnion([Q1]), "revolveType" : RevolveType.FULL});
        }
        {
            var Q0;
            Q0=makeQuery(id+"F36.imprint","IMPRINT",FACE,{"disambiguationData":[TD([[makeQuery(id+"F36.imprint","IMPRINT",EDGE,{"derivedFrom":sQuery(id+"F36.wireOp",EDGE,"E119.9.0.0")}),-1.0]])]});
            var Q1;
            Q1=sQuery(id+"F36.wireOp",EDGE,"E119.9.0.0");
            revolve(context, id + "F46", {"entities" : qUnion([Q0]), "axis" : qUnion([Q1]), "revolveType" : RevolveType.FULL});
        }
        {
            var Q0;
            Q0=makeQuery(id+"F36.imprint","IMPRINT",FACE,{"disambiguationData":[TD([[makeQuery(id+"F36.imprint","IMPRINT",EDGE,{"derivedFrom":sQuery(id+"F36.wireOp",EDGE,"E119.10.0.0")}),-1.0]])]});
            var Q1;
            Q1=sQuery(id+"F36.wireOp",EDGE,"E119.10.0.0");
            revolve(context, id + "F47", {"entities" : qUnion([Q0]), "axis" : qUnion([Q1]), "revolveType" : RevolveType.FULL});
        }
        {
            var Q0;
            Q0=makeQuery(id+"F36.imprint","IMPRINT",FACE,{"disambiguationData":[TD([[makeQuery(id+"F36.imprint","IMPRINT",EDGE,{"derivedFrom":sQuery(id+"F36.wireOp",EDGE,"E119.11.0.0")}),-1.0]])]});
            var Q1;
            Q1=sQuery(id+"F36.wireOp",EDGE,"E119.11.0.0");
            revolve(context, id + "F48", {"entities" : qUnion([Q0]), "axis" : qUnion([Q1]), "revolveType" : RevolveType.FULL});
        }
        {
            var Q0;
            Q0=qCreatedBy(makeId("Top.planeOp"),FACE);
            var sketch = newSketch(context, id + "F49", { "sketchPlane" : qUnion([Q0])});
            skLineSegment(sketch, "E153", {"start": v(0, 0) * mm, "end": v(0, -10) * mm, "construction": true});
            skLineSegment(sketch, "E154", {"start": v(0, -10) * mm, "end": v(0, -20) * mm, "construction": true});
            skLineSegment(sketch, "E155", {"start": v(0, -20) * mm, "end": v(0, -30) * mm, "construction": true});
            skCircle(sketch, "E156.cCircle", {"center": v(0, -10) * mm, "radius": 1.25 * mm, "construction": true});
            skLineSegment(sketch, "E156.0", {"start": v(-0.72, -8.75) * mm, "end": v(0.72, -8.75) * mm});
            skLineSegment(sketch, "E156.1", {"start": v(0.72, -8.75) * mm, "end": v(1.44, -10) * mm});
            skLineSegment(sketch, "E156.2", {"start": v(1.44, -10) * mm, "end": v(0.72, -11.25) * mm});
            skLineSegment(sketch, "E156.3", {"start": v(0.72, -11.25) * mm, "end": v(-0.72, -11.25) * mm});
            skLineSegment(sketch, "E156.4", {"start": v(-0.72, -11.25) * mm, "end": v(-1.44, -10) * mm});
            skLineSegment(sketch, "E156.5", {"start": v(-1.44, -10) * mm, "end": v(-0.72, -8.75) * mm});
            skPoint(sketch, "E156.0.midPoint", {"position": v(0, -8.75) * mm});
            skCircle(sketch, "E157.cCircle", {"center": v(0, -20) * mm, "radius": 1.5 * mm, "construction": true});
            skLineSegment(sketch, "E157.0", {"start": v(-0.87, -18.5) * mm, "end": v(0.87, -18.5) * mm});
            skLineSegment(sketch, "E157.1", {"start": v(0.87, -18.5) * mm, "end": v(1.73, -20) * mm});
            skLineSegment(sketch, "E157.2", {"start": v(1.73, -20) * mm, "end": v(0.87, -21.5) * mm});
            skLineSegment(sketch, "E157.3", {"start": v(0.87, -21.5) * mm, "end": v(-0.87, -21.5) * mm});
            skLineSegment(sketch, "E157.4", {"start": v(-0.87, -21.5) * mm, "end": v(-1.73, -20) * mm});
            skLineSegment(sketch, "E157.5", {"start": v(-1.73, -20) * mm, "end": v(-0.87, -18.5) * mm});
            skPoint(sketch, "E157.0.midPoint", {"position": v(0, -18.5) * mm});
            skCircle(sketch, "E158.cCircle", {"center": v(0, -30) * mm, "radius": 2 * mm, "construction": true});
            skLineSegment(sketch, "E158.0", {"start": v(-1.15, -28) * mm, "end": v(1.15, -28) * mm});
            skLineSegment(sketch, "E158.1", {"start": v(1.15, -28) * mm, "end": v(2.3, -30) * mm});
            skLineSegment(sketch, "E158.2", {"start": v(2.3, -30) * mm, "end": v(1.15, -32) * mm});
            skLineSegment(sketch, "E158.3", {"start": v(1.15, -32) * mm, "end": v(-1.15, -32) * mm});
            skLineSegment(sketch, "E158.4", {"start": v(-1.15, -32) * mm, "end": v(-2.3, -30) * mm});
            skLineSegment(sketch, "E158.5", {"start": v(-2.3, -30) * mm, "end": v(-1.15, -28) * mm});
            skPoint(sketch, "E158.0.midPoint", {"position": v(0, -28) * mm});
            skPoint(sketch, "E159.1.0.0", {"position": v(10, -8.75) * mm});
            skLineSegment(sketch, "E159.1.0.1", {"start": v(10.72, -11.25) * mm, "end": v(9.28, -11.25) * mm});
            skLineSegment(sketch, "E159.1.0.2", {"start": v(10.87, -21.5) * mm, "end": v(9.13, -21.5) * mm});
            skLineSegment(sketch, "E159.1.0.3", {"start": v(9.13, -18.5) * mm, "end": v(10.87, -18.5) * mm});
            skLineSegment(sketch, "E159.1.0.4", {"start": v(8.56, -10) * mm, "end": v(9.28, -8.75) * mm});
            skLineSegment(sketch, "E159.1.0.5", {"start": v(11.15, -32) * mm, "end": v(8.85, -32) * mm});
            skPoint(sketch, "E159.1.0.6", {"position": v(10, -18.5) * mm});
            skLineSegment(sketch, "E159.1.0.7", {"start": v(8.85, -28) * mm, "end": v(11.15, -28) * mm});
            skPoint(sketch, "E159.1.0.8", {"position": v(10, -28) * mm});
            skLineSegment(sketch, "E159.1.0.9", {"start": v(9.28, -11.25) * mm, "end": v(8.56, -10) * mm});
            skLineSegment(sketch, "E159.1.0.10", {"start": v(9.28, -8.75) * mm, "end": v(10.72, -8.75) * mm});
            skLineSegment(sketch, "E159.1.0.11", {"start": v(8.85, -32) * mm, "end": v(7.7, -30) * mm});
            skLineSegment(sketch, "E159.1.0.12", {"start": v(11.44, -10) * mm, "end": v(10.72, -11.25) * mm});
            skLineSegment(sketch, "E159.1.0.13", {"start": v(12.3, -30) * mm, "end": v(11.15, -32) * mm});
            skLineSegment(sketch, "E159.1.0.14", {"start": v(11.15, -28) * mm, "end": v(12.3, -30) * mm});
            skCircle(sketch, "E159.1.0.15", {"center": v(10, -30) * mm, "radius": 2 * mm, "construction": true});
            skLineSegment(sketch, "E159.1.0.16", {"start": v(11.73, -20) * mm, "end": v(10.87, -21.5) * mm});
            skLineSegment(sketch, "E159.1.0.17", {"start": v(8.27, -20) * mm, "end": v(9.13, -18.5) * mm});
            skLineSegment(sketch, "E159.1.0.18", {"start": v(7.7, -30) * mm, "end": v(8.85, -28) * mm});
            skCircle(sketch, "E159.1.0.19", {"center": v(10, -10) * mm, "radius": 1.25 * mm, "construction": true});
            skLineSegment(sketch, "E159.1.0.20", {"start": v(9.13, -21.5) * mm, "end": v(8.27, -20) * mm});
            skLineSegment(sketch, "E159.1.0.21", {"start": v(10.87, -18.5) * mm, "end": v(11.73, -20) * mm});
            skCircle(sketch, "E159.1.0.22", {"center": v(10, -20) * mm, "radius": 1.5 * mm, "construction": true});
            skLineSegment(sketch, "E159.1.0.23", {"start": v(10.72, -8.75) * mm, "end": v(11.44, -10) * mm});
            skPoint(sketch, "E159.2.0.0", {"position": v(20, -8.75) * mm});
            skLineSegment(sketch, "E159.2.0.1", {"start": v(20.72, -11.25) * mm, "end": v(19.28, -11.25) * mm});
            skLineSegment(sketch, "E159.2.0.2", {"start": v(20.87, -21.5) * mm, "end": v(19.13, -21.5) * mm});
            skLineSegment(sketch, "E159.2.0.3", {"start": v(19.13, -18.5) * mm, "end": v(20.87, -18.5) * mm});
            skLineSegment(sketch, "E159.2.0.4", {"start": v(18.56, -10) * mm, "end": v(19.28, -8.75) * mm});
            skLineSegment(sketch, "E159.2.0.5", {"start": v(21.15, -32) * mm, "end": v(18.85, -32) * mm});
            skPoint(sketch, "E159.2.0.6", {"position": v(20, -18.5) * mm});
            skLineSegment(sketch, "E159.2.0.7", {"start": v(18.85, -28) * mm, "end": v(21.15, -28) * mm});
            skPoint(sketch, "E159.2.0.8", {"position": v(20, -28) * mm});
            skLineSegment(sketch, "E159.2.0.9", {"start": v(19.28, -11.25) * mm, "end": v(18.56, -10) * mm});
            skLineSegment(sketch, "E159.2.0.10", {"start": v(19.28, -8.75) * mm, "end": v(20.72, -8.75) * mm});
            skLineSegment(sketch, "E159.2.0.11", {"start": v(18.85, -32) * mm, "end": v(17.7, -30) * mm});
            skLineSegment(sketch, "E159.2.0.12", {"start": v(21.44, -10) * mm, "end": v(20.72, -11.25) * mm});
            skLineSegment(sketch, "E159.2.0.13", {"start": v(22.3, -30) * mm, "end": v(21.15, -32) * mm});
            skLineSegment(sketch, "E159.2.0.14", {"start": v(21.15, -28) * mm, "end": v(22.3, -30) * mm});
            skCircle(sketch, "E159.2.0.15", {"center": v(20, -30) * mm, "radius": 2 * mm, "construction": true});
            skLineSegment(sketch, "E159.2.0.16", {"start": v(21.73, -20) * mm, "end": v(20.87, -21.5) * mm});
            skLineSegment(sketch, "E159.2.0.17", {"start": v(18.27, -20) * mm, "end": v(19.13, -18.5) * mm});
            skLineSegment(sketch, "E159.2.0.18", {"start": v(17.7, -30) * mm, "end": v(18.85, -28) * mm});
            skCircle(sketch, "E159.2.0.19", {"center": v(20, -10) * mm, "radius": 1.25 * mm, "construction": true});
            skLineSegment(sketch, "E159.2.0.20", {"start": v(19.13, -21.5) * mm, "end": v(18.27, -20) * mm});
            skLineSegment(sketch, "E159.2.0.21", {"start": v(20.87, -18.5) * mm, "end": v(21.73, -20) * mm});
            skCircle(sketch, "E159.2.0.22", {"center": v(20, -20) * mm, "radius": 1.5 * mm, "construction": true});
            skLineSegment(sketch, "E159.2.0.23", {"start": v(20.72, -8.75) * mm, "end": v(21.44, -10) * mm});
            skPoint(sketch, "E159.3.0.0", {"position": v(30, -8.75) * mm});
            skLineSegment(sketch, "E159.3.0.1", {"start": v(30.72, -11.25) * mm, "end": v(29.28, -11.25) * mm});
            skLineSegment(sketch, "E159.3.0.2", {"start": v(30.87, -21.5) * mm, "end": v(29.13, -21.5) * mm});
            skLineSegment(sketch, "E159.3.0.3", {"start": v(29.13, -18.5) * mm, "end": v(30.87, -18.5) * mm});
            skLineSegment(sketch, "E159.3.0.4", {"start": v(28.56, -10) * mm, "end": v(29.28, -8.75) * mm});
            skLineSegment(sketch, "E159.3.0.5", {"start": v(31.15, -32) * mm, "end": v(28.85, -32) * mm});
            skPoint(sketch, "E159.3.0.6", {"position": v(30, -18.5) * mm});
            skLineSegment(sketch, "E159.3.0.7", {"start": v(28.85, -28) * mm, "end": v(31.15, -28) * mm});
            skPoint(sketch, "E159.3.0.8", {"position": v(30, -28) * mm});
            skLineSegment(sketch, "E159.3.0.9", {"start": v(29.28, -11.25) * mm, "end": v(28.56, -10) * mm});
            skLineSegment(sketch, "E159.3.0.10", {"start": v(29.28, -8.75) * mm, "end": v(30.72, -8.75) * mm});
            skLineSegment(sketch, "E159.3.0.11", {"start": v(28.85, -32) * mm, "end": v(27.7, -30) * mm});
            skLineSegment(sketch, "E159.3.0.12", {"start": v(31.44, -10) * mm, "end": v(30.72, -11.25) * mm});
            skLineSegment(sketch, "E159.3.0.13", {"start": v(32.3, -30) * mm, "end": v(31.15, -32) * mm});
            skLineSegment(sketch, "E159.3.0.14", {"start": v(31.15, -28) * mm, "end": v(32.3, -30) * mm});
            skCircle(sketch, "E159.3.0.15", {"center": v(30, -30) * mm, "radius": 2 * mm, "construction": true});
            skLineSegment(sketch, "E159.3.0.16", {"start": v(31.73, -20) * mm, "end": v(30.87, -21.5) * mm});
            skLineSegment(sketch, "E159.3.0.17", {"start": v(28.27, -20) * mm, "end": v(29.13, -18.5) * mm});
            skLineSegment(sketch, "E159.3.0.18", {"start": v(27.7, -30) * mm, "end": v(28.85, -28) * mm});
            skCircle(sketch, "E159.3.0.19", {"center": v(30, -10) * mm, "radius": 1.25 * mm, "construction": true});
            skLineSegment(sketch, "E159.3.0.20", {"start": v(29.13, -21.5) * mm, "end": v(28.27, -20) * mm});
            skLineSegment(sketch, "E159.3.0.21", {"start": v(30.87, -18.5) * mm, "end": v(31.73, -20) * mm});
            skCircle(sketch, "E159.3.0.22", {"center": v(30, -20) * mm, "radius": 1.5 * mm, "construction": true});
            skLineSegment(sketch, "E159.3.0.23", {"start": v(30.72, -8.75) * mm, "end": v(31.44, -10) * mm});
            skPoint(sketch, "E159.4.0.0", {"position": v(40, -8.75) * mm});
            skLineSegment(sketch, "E159.4.0.1", {"start": v(40.72, -11.25) * mm, "end": v(39.28, -11.25) * mm});
            skLineSegment(sketch, "E159.4.0.2", {"start": v(40.87, -21.5) * mm, "end": v(39.13, -21.5) * mm});
            skLineSegment(sketch, "E159.4.0.3", {"start": v(39.13, -18.5) * mm, "end": v(40.87, -18.5) * mm});
            skLineSegment(sketch, "E159.4.0.4", {"start": v(38.56, -10) * mm, "end": v(39.28, -8.75) * mm});
            skLineSegment(sketch, "E159.4.0.5", {"start": v(41.15, -32) * mm, "end": v(38.85, -32) * mm});
            skPoint(sketch, "E159.4.0.6", {"position": v(40, -18.5) * mm});
            skLineSegment(sketch, "E159.4.0.7", {"start": v(38.85, -28) * mm, "end": v(41.15, -28) * mm});
            skPoint(sketch, "E159.4.0.8", {"position": v(40, -28) * mm});
            skLineSegment(sketch, "E159.4.0.9", {"start": v(39.28, -11.25) * mm, "end": v(38.56, -10) * mm});
            skLineSegment(sketch, "E159.4.0.10", {"start": v(39.28, -8.75) * mm, "end": v(40.72, -8.75) * mm});
            skLineSegment(sketch, "E159.4.0.11", {"start": v(38.85, -32) * mm, "end": v(37.7, -30) * mm});
            skLineSegment(sketch, "E159.4.0.12", {"start": v(41.44, -10) * mm, "end": v(40.72, -11.25) * mm});
            skLineSegment(sketch, "E159.4.0.13", {"start": v(42.3, -30) * mm, "end": v(41.15, -32) * mm});
            skLineSegment(sketch, "E159.4.0.14", {"start": v(41.15, -28) * mm, "end": v(42.3, -30) * mm});
            skCircle(sketch, "E159.4.0.15", {"center": v(40, -30) * mm, "radius": 2 * mm, "construction": true});
            skLineSegment(sketch, "E159.4.0.16", {"start": v(41.73, -20) * mm, "end": v(40.87, -21.5) * mm});
            skLineSegment(sketch, "E159.4.0.17", {"start": v(38.27, -20) * mm, "end": v(39.13, -18.5) * mm});
            skLineSegment(sketch, "E159.4.0.18", {"start": v(37.7, -30) * mm, "end": v(38.85, -28) * mm});
            skCircle(sketch, "E159.4.0.19", {"center": v(40, -10) * mm, "radius": 1.25 * mm, "construction": true});
            skLineSegment(sketch, "E159.4.0.20", {"start": v(39.13, -21.5) * mm, "end": v(38.27, -20) * mm});
            skLineSegment(sketch, "E159.4.0.21", {"start": v(40.87, -18.5) * mm, "end": v(41.73, -20) * mm});
            skCircle(sketch, "E159.4.0.22", {"center": v(40, -20) * mm, "radius": 1.5 * mm, "construction": true});
            skLineSegment(sketch, "E159.4.0.23", {"start": v(40.72, -8.75) * mm, "end": v(41.44, -10) * mm});
            skPoint(sketch, "E159.5.0.0", {"position": v(50, -8.75) * mm});
            skLineSegment(sketch, "E159.5.0.1", {"start": v(50.72, -11.25) * mm, "end": v(49.28, -11.25) * mm});
            skLineSegment(sketch, "E159.5.0.2", {"start": v(50.87, -21.5) * mm, "end": v(49.13, -21.5) * mm});
            skLineSegment(sketch, "E159.5.0.3", {"start": v(49.13, -18.5) * mm, "end": v(50.87, -18.5) * mm});
            skLineSegment(sketch, "E159.5.0.4", {"start": v(48.56, -10) * mm, "end": v(49.28, -8.75) * mm});
            skLineSegment(sketch, "E159.5.0.5", {"start": v(51.15, -32) * mm, "end": v(48.85, -32) * mm});
            skPoint(sketch, "E159.5.0.6", {"position": v(50, -18.5) * mm});
            skLineSegment(sketch, "E159.5.0.7", {"start": v(48.85, -28) * mm, "end": v(51.15, -28) * mm});
            skPoint(sketch, "E159.5.0.8", {"position": v(50, -28) * mm});
            skLineSegment(sketch, "E159.5.0.9", {"start": v(49.28, -11.25) * mm, "end": v(48.56, -10) * mm});
            skLineSegment(sketch, "E159.5.0.10", {"start": v(49.28, -8.75) * mm, "end": v(50.72, -8.75) * mm});
            skLineSegment(sketch, "E159.5.0.11", {"start": v(48.85, -32) * mm, "end": v(47.7, -30) * mm});
            skLineSegment(sketch, "E159.5.0.12", {"start": v(51.44, -10) * mm, "end": v(50.72, -11.25) * mm});
            skLineSegment(sketch, "E159.5.0.13", {"start": v(52.3, -30) * mm, "end": v(51.15, -32) * mm});
            skLineSegment(sketch, "E159.5.0.14", {"start": v(51.15, -28) * mm, "end": v(52.3, -30) * mm});
            skCircle(sketch, "E159.5.0.15", {"center": v(50, -30) * mm, "radius": 2 * mm, "construction": true});
            skLineSegment(sketch, "E159.5.0.16", {"start": v(51.73, -20) * mm, "end": v(50.87, -21.5) * mm});
            skLineSegment(sketch, "E159.5.0.17", {"start": v(48.27, -20) * mm, "end": v(49.13, -18.5) * mm});
            skLineSegment(sketch, "E159.5.0.18", {"start": v(47.7, -30) * mm, "end": v(48.85, -28) * mm});
            skCircle(sketch, "E159.5.0.19", {"center": v(50, -10) * mm, "radius": 1.25 * mm, "construction": true});
            skLineSegment(sketch, "E159.5.0.20", {"start": v(49.13, -21.5) * mm, "end": v(48.27, -20) * mm});
            skLineSegment(sketch, "E159.5.0.21", {"start": v(50.87, -18.5) * mm, "end": v(51.73, -20) * mm});
            skCircle(sketch, "E159.5.0.22", {"center": v(50, -20) * mm, "radius": 1.5 * mm, "construction": true});
            skLineSegment(sketch, "E159.5.0.23", {"start": v(50.72, -8.75) * mm, "end": v(51.44, -10) * mm});
            skPoint(sketch, "E159.6.0.0", {"position": v(60, -8.75) * mm});
            skLineSegment(sketch, "E159.6.0.1", {"start": v(60.72, -11.25) * mm, "end": v(59.28, -11.25) * mm});
            skLineSegment(sketch, "E159.6.0.2", {"start": v(60.87, -21.5) * mm, "end": v(59.13, -21.5) * mm});
            skLineSegment(sketch, "E159.6.0.3", {"start": v(59.13, -18.5) * mm, "end": v(60.87, -18.5) * mm});
            skLineSegment(sketch, "E159.6.0.4", {"start": v(58.56, -10) * mm, "end": v(59.28, -8.75) * mm});
            skLineSegment(sketch, "E159.6.0.5", {"start": v(61.15, -32) * mm, "end": v(58.85, -32) * mm});
            skPoint(sketch, "E159.6.0.6", {"position": v(60, -18.5) * mm});
            skLineSegment(sketch, "E159.6.0.7", {"start": v(58.85, -28) * mm, "end": v(61.15, -28) * mm});
            skPoint(sketch, "E159.6.0.8", {"position": v(60, -28) * mm});
            skLineSegment(sketch, "E159.6.0.9", {"start": v(59.28, -11.25) * mm, "end": v(58.56, -10) * mm});
            skLineSegment(sketch, "E159.6.0.10", {"start": v(59.28, -8.75) * mm, "end": v(60.72, -8.75) * mm});
            skLineSegment(sketch, "E159.6.0.11", {"start": v(58.85, -32) * mm, "end": v(57.7, -30) * mm});
            skLineSegment(sketch, "E159.6.0.12", {"start": v(61.44, -10) * mm, "end": v(60.72, -11.25) * mm});
            skLineSegment(sketch, "E159.6.0.13", {"start": v(62.3, -30) * mm, "end": v(61.15, -32) * mm});
            skLineSegment(sketch, "E159.6.0.14", {"start": v(61.15, -28) * mm, "end": v(62.3, -30) * mm});
            skCircle(sketch, "E159.6.0.15", {"center": v(60, -30) * mm, "radius": 2 * mm, "construction": true});
            skLineSegment(sketch, "E159.6.0.16", {"start": v(61.73, -20) * mm, "end": v(60.87, -21.5) * mm});
            skLineSegment(sketch, "E159.6.0.17", {"start": v(58.27, -20) * mm, "end": v(59.13, -18.5) * mm});
            skLineSegment(sketch, "E159.6.0.18", {"start": v(57.7, -30) * mm, "end": v(58.85, -28) * mm});
            skCircle(sketch, "E159.6.0.19", {"center": v(60, -10) * mm, "radius": 1.25 * mm, "construction": true});
            skLineSegment(sketch, "E159.6.0.20", {"start": v(59.13, -21.5) * mm, "end": v(58.27, -20) * mm});
            skLineSegment(sketch, "E159.6.0.21", {"start": v(60.87, -18.5) * mm, "end": v(61.73, -20) * mm});
            skCircle(sketch, "E159.6.0.22", {"center": v(60, -20) * mm, "radius": 1.5 * mm, "construction": true});
            skLineSegment(sketch, "E159.6.0.23", {"start": v(60.72, -8.75) * mm, "end": v(61.44, -10) * mm});
            skPoint(sketch, "E159.7.0.0", {"position": v(70, -8.75) * mm});
            skLineSegment(sketch, "E159.7.0.1", {"start": v(70.72, -11.25) * mm, "end": v(69.28, -11.25) * mm});
            skLineSegment(sketch, "E159.7.0.2", {"start": v(70.87, -21.5) * mm, "end": v(69.13, -21.5) * mm});
            skLineSegment(sketch, "E159.7.0.3", {"start": v(69.13, -18.5) * mm, "end": v(70.87, -18.5) * mm});
            skLineSegment(sketch, "E159.7.0.4", {"start": v(68.56, -10) * mm, "end": v(69.28, -8.75) * mm});
            skLineSegment(sketch, "E159.7.0.5", {"start": v(71.15, -32) * mm, "end": v(68.85, -32) * mm});
            skPoint(sketch, "E159.7.0.6", {"position": v(70, -18.5) * mm});
            skLineSegment(sketch, "E159.7.0.7", {"start": v(68.85, -28) * mm, "end": v(71.15, -28) * mm});
            skPoint(sketch, "E159.7.0.8", {"position": v(70, -28) * mm});
            skLineSegment(sketch, "E159.7.0.9", {"start": v(69.28, -11.25) * mm, "end": v(68.56, -10) * mm});
            skLineSegment(sketch, "E159.7.0.10", {"start": v(69.28, -8.75) * mm, "end": v(70.72, -8.75) * mm});
            skLineSegment(sketch, "E159.7.0.11", {"start": v(68.85, -32) * mm, "end": v(67.7, -30) * mm});
            skLineSegment(sketch, "E159.7.0.12", {"start": v(71.44, -10) * mm, "end": v(70.72, -11.25) * mm});
            skLineSegment(sketch, "E159.7.0.13", {"start": v(72.3, -30) * mm, "end": v(71.15, -32) * mm});
            skLineSegment(sketch, "E159.7.0.14", {"start": v(71.15, -28) * mm, "end": v(72.3, -30) * mm});
            skCircle(sketch, "E159.7.0.15", {"center": v(70, -30) * mm, "radius": 2 * mm, "construction": true});
            skLineSegment(sketch, "E159.7.0.16", {"start": v(71.73, -20) * mm, "end": v(70.87, -21.5) * mm});
            skLineSegment(sketch, "E159.7.0.17", {"start": v(68.27, -20) * mm, "end": v(69.13, -18.5) * mm});
            skLineSegment(sketch, "E159.7.0.18", {"start": v(67.7, -30) * mm, "end": v(68.85, -28) * mm});
            skCircle(sketch, "E159.7.0.19", {"center": v(70, -10) * mm, "radius": 1.25 * mm, "construction": true});
            skLineSegment(sketch, "E159.7.0.20", {"start": v(69.13, -21.5) * mm, "end": v(68.27, -20) * mm});
            skLineSegment(sketch, "E159.7.0.21", {"start": v(70.87, -18.5) * mm, "end": v(71.73, -20) * mm});
            skCircle(sketch, "E159.7.0.22", {"center": v(70, -20) * mm, "radius": 1.5 * mm, "construction": true});
            skLineSegment(sketch, "E159.7.0.23", {"start": v(70.72, -8.75) * mm, "end": v(71.44, -10) * mm});
            skPoint(sketch, "E159.8.0.0", {"position": v(80, -8.75) * mm});
            skLineSegment(sketch, "E159.8.0.1", {"start": v(80.72, -11.25) * mm, "end": v(79.28, -11.25) * mm});
            skLineSegment(sketch, "E159.8.0.2", {"start": v(80.87, -21.5) * mm, "end": v(79.13, -21.5) * mm});
            skLineSegment(sketch, "E159.8.0.3", {"start": v(79.13, -18.5) * mm, "end": v(80.87, -18.5) * mm});
            skLineSegment(sketch, "E159.8.0.4", {"start": v(78.56, -10) * mm, "end": v(79.28, -8.75) * mm});
            skLineSegment(sketch, "E159.8.0.5", {"start": v(81.15, -32) * mm, "end": v(78.85, -32) * mm});
            skPoint(sketch, "E159.8.0.6", {"position": v(80, -18.5) * mm});
            skLineSegment(sketch, "E159.8.0.7", {"start": v(78.85, -28) * mm, "end": v(81.15, -28) * mm});
            skPoint(sketch, "E159.8.0.8", {"position": v(80, -28) * mm});
            skLineSegment(sketch, "E159.8.0.9", {"start": v(79.28, -11.25) * mm, "end": v(78.56, -10) * mm});
            skLineSegment(sketch, "E159.8.0.10", {"start": v(79.28, -8.75) * mm, "end": v(80.72, -8.75) * mm});
            skLineSegment(sketch, "E159.8.0.11", {"start": v(78.85, -32) * mm, "end": v(77.7, -30) * mm});
            skLineSegment(sketch, "E159.8.0.12", {"start": v(81.44, -10) * mm, "end": v(80.72, -11.25) * mm});
            skLineSegment(sketch, "E159.8.0.13", {"start": v(82.3, -30) * mm, "end": v(81.15, -32) * mm});
            skLineSegment(sketch, "E159.8.0.14", {"start": v(81.15, -28) * mm, "end": v(82.3, -30) * mm});
            skCircle(sketch, "E159.8.0.15", {"center": v(80, -30) * mm, "radius": 2 * mm, "construction": true});
            skLineSegment(sketch, "E159.8.0.16", {"start": v(81.73, -20) * mm, "end": v(80.87, -21.5) * mm});
            skLineSegment(sketch, "E159.8.0.17", {"start": v(78.27, -20) * mm, "end": v(79.13, -18.5) * mm});
            skLineSegment(sketch, "E159.8.0.18", {"start": v(77.7, -30) * mm, "end": v(78.85, -28) * mm});
            skCircle(sketch, "E159.8.0.19", {"center": v(80, -10) * mm, "radius": 1.25 * mm, "construction": true});
            skLineSegment(sketch, "E159.8.0.20", {"start": v(79.13, -21.5) * mm, "end": v(78.27, -20) * mm});
            skLineSegment(sketch, "E159.8.0.21", {"start": v(80.87, -18.5) * mm, "end": v(81.73, -20) * mm});
            skCircle(sketch, "E159.8.0.22", {"center": v(80, -20) * mm, "radius": 1.5 * mm, "construction": true});
            skLineSegment(sketch, "E159.8.0.23", {"start": v(80.72, -8.75) * mm, "end": v(81.44, -10) * mm});
            skPoint(sketch, "E159.9.0.0", {"position": v(90, -8.75) * mm});
            skLineSegment(sketch, "E159.9.0.1", {"start": v(90.72, -11.25) * mm, "end": v(89.28, -11.25) * mm});
            skLineSegment(sketch, "E159.9.0.2", {"start": v(90.87, -21.5) * mm, "end": v(89.13, -21.5) * mm});
            skLineSegment(sketch, "E159.9.0.3", {"start": v(89.13, -18.5) * mm, "end": v(90.87, -18.5) * mm});
            skLineSegment(sketch, "E159.9.0.4", {"start": v(88.56, -10) * mm, "end": v(89.28, -8.75) * mm});
            skLineSegment(sketch, "E159.9.0.5", {"start": v(91.15, -32) * mm, "end": v(88.85, -32) * mm});
            skPoint(sketch, "E159.9.0.6", {"position": v(90, -18.5) * mm});
            skLineSegment(sketch, "E159.9.0.7", {"start": v(88.85, -28) * mm, "end": v(91.15, -28) * mm});
            skPoint(sketch, "E159.9.0.8", {"position": v(90, -28) * mm});
            skLineSegment(sketch, "E159.9.0.9", {"start": v(89.28, -11.25) * mm, "end": v(88.56, -10) * mm});
            skLineSegment(sketch, "E159.9.0.10", {"start": v(89.28, -8.75) * mm, "end": v(90.72, -8.75) * mm});
            skLineSegment(sketch, "E159.9.0.11", {"start": v(88.85, -32) * mm, "end": v(87.7, -30) * mm});
            skLineSegment(sketch, "E159.9.0.12", {"start": v(91.44, -10) * mm, "end": v(90.72, -11.25) * mm});
            skLineSegment(sketch, "E159.9.0.13", {"start": v(92.3, -30) * mm, "end": v(91.15, -32) * mm});
            skLineSegment(sketch, "E159.9.0.14", {"start": v(91.15, -28) * mm, "end": v(92.3, -30) * mm});
            skCircle(sketch, "E159.9.0.15", {"center": v(90, -30) * mm, "radius": 2 * mm, "construction": true});
            skLineSegment(sketch, "E159.9.0.16", {"start": v(91.73, -20) * mm, "end": v(90.87, -21.5) * mm});
            skLineSegment(sketch, "E159.9.0.17", {"start": v(88.27, -20) * mm, "end": v(89.13, -18.5) * mm});
            skLineSegment(sketch, "E159.9.0.18", {"start": v(87.7, -30) * mm, "end": v(88.85, -28) * mm});
            skCircle(sketch, "E159.9.0.19", {"center": v(90, -10) * mm, "radius": 1.25 * mm, "construction": true});
            skLineSegment(sketch, "E159.9.0.20", {"start": v(89.13, -21.5) * mm, "end": v(88.27, -20) * mm});
            skLineSegment(sketch, "E159.9.0.21", {"start": v(90.87, -18.5) * mm, "end": v(91.73, -20) * mm});
            skCircle(sketch, "E159.9.0.22", {"center": v(90, -20) * mm, "radius": 1.5 * mm, "construction": true});
            skLineSegment(sketch, "E159.9.0.23", {"start": v(90.72, -8.75) * mm, "end": v(91.44, -10) * mm});
            skPoint(sketch, "E159.10.0.0", {"position": v(100, -8.75) * mm});
            skLineSegment(sketch, "E159.10.0.1", {"start": v(100.72, -11.25) * mm, "end": v(99.28, -11.25) * mm});
            skLineSegment(sketch, "E159.10.0.2", {"start": v(100.87, -21.5) * mm, "end": v(99.13, -21.5) * mm});
            skLineSegment(sketch, "E159.10.0.3", {"start": v(99.13, -18.5) * mm, "end": v(100.87, -18.5) * mm});
            skLineSegment(sketch, "E159.10.0.4", {"start": v(98.56, -10) * mm, "end": v(99.28, -8.75) * mm});
            skLineSegment(sketch, "E159.10.0.5", {"start": v(101.15, -32) * mm, "end": v(98.85, -32) * mm});
            skPoint(sketch, "E159.10.0.6", {"position": v(100, -18.5) * mm});
            skLineSegment(sketch, "E159.10.0.7", {"start": v(98.85, -28) * mm, "end": v(101.15, -28) * mm});
            skPoint(sketch, "E159.10.0.8", {"position": v(100, -28) * mm});
            skLineSegment(sketch, "E159.10.0.9", {"start": v(99.28, -11.25) * mm, "end": v(98.56, -10) * mm});
            skLineSegment(sketch, "E159.10.0.10", {"start": v(99.28, -8.75) * mm, "end": v(100.72, -8.75) * mm});
            skLineSegment(sketch, "E159.10.0.11", {"start": v(98.85, -32) * mm, "end": v(97.7, -30) * mm});
            skLineSegment(sketch, "E159.10.0.12", {"start": v(101.44, -10) * mm, "end": v(100.72, -11.25) * mm});
            skLineSegment(sketch, "E159.10.0.13", {"start": v(102.3, -30) * mm, "end": v(101.15, -32) * mm});
            skLineSegment(sketch, "E159.10.0.14", {"start": v(101.15, -28) * mm, "end": v(102.3, -30) * mm});
            skCircle(sketch, "E159.10.0.15", {"center": v(100, -30) * mm, "radius": 2 * mm, "construction": true});
            skLineSegment(sketch, "E159.10.0.16", {"start": v(101.73, -20) * mm, "end": v(100.87, -21.5) * mm});
            skLineSegment(sketch, "E159.10.0.17", {"start": v(98.27, -20) * mm, "end": v(99.13, -18.5) * mm});
            skLineSegment(sketch, "E159.10.0.18", {"start": v(97.7, -30) * mm, "end": v(98.85, -28) * mm});
            skCircle(sketch, "E159.10.0.19", {"center": v(100, -10) * mm, "radius": 1.25 * mm, "construction": true});
            skLineSegment(sketch, "E159.10.0.20", {"start": v(99.13, -21.5) * mm, "end": v(98.27, -20) * mm});
            skLineSegment(sketch, "E159.10.0.21", {"start": v(100.87, -18.5) * mm, "end": v(101.73, -20) * mm});
            skCircle(sketch, "E159.10.0.22", {"center": v(100, -20) * mm, "radius": 1.5 * mm, "construction": true});
            skLineSegment(sketch, "E159.10.0.23", {"start": v(100.72, -8.75) * mm, "end": v(101.44, -10) * mm});
            skPoint(sketch, "E159.11.0.0", {"position": v(110, -8.75) * mm});
            skLineSegment(sketch, "E159.11.0.1", {"start": v(110.72, -11.25) * mm, "end": v(109.28, -11.25) * mm});
            skLineSegment(sketch, "E159.11.0.2", {"start": v(110.87, -21.5) * mm, "end": v(109.13, -21.5) * mm});
            skLineSegment(sketch, "E159.11.0.3", {"start": v(109.13, -18.5) * mm, "end": v(110.87, -18.5) * mm});
            skLineSegment(sketch, "E159.11.0.4", {"start": v(108.56, -10) * mm, "end": v(109.28, -8.75) * mm});
            skLineSegment(sketch, "E159.11.0.5", {"start": v(111.15, -32) * mm, "end": v(108.85, -32) * mm});
            skPoint(sketch, "E159.11.0.6", {"position": v(110, -18.5) * mm});
            skLineSegment(sketch, "E159.11.0.7", {"start": v(108.85, -28) * mm, "end": v(111.15, -28) * mm});
            skPoint(sketch, "E159.11.0.8", {"position": v(110, -28) * mm});
            skLineSegment(sketch, "E159.11.0.9", {"start": v(109.28, -11.25) * mm, "end": v(108.56, -10) * mm});
            skLineSegment(sketch, "E159.11.0.10", {"start": v(109.28, -8.75) * mm, "end": v(110.72, -8.75) * mm});
            skLineSegment(sketch, "E159.11.0.11", {"start": v(108.85, -32) * mm, "end": v(107.7, -30) * mm});
            skLineSegment(sketch, "E159.11.0.12", {"start": v(111.44, -10) * mm, "end": v(110.72, -11.25) * mm});
            skLineSegment(sketch, "E159.11.0.13", {"start": v(112.3, -30) * mm, "end": v(111.15, -32) * mm});
            skLineSegment(sketch, "E159.11.0.14", {"start": v(111.15, -28) * mm, "end": v(112.3, -30) * mm});
            skCircle(sketch, "E159.11.0.15", {"center": v(110, -30) * mm, "radius": 2 * mm, "construction": true});
            skLineSegment(sketch, "E159.11.0.16", {"start": v(111.73, -20) * mm, "end": v(110.87, -21.5) * mm});
            skLineSegment(sketch, "E159.11.0.17", {"start": v(108.27, -20) * mm, "end": v(109.13, -18.5) * mm});
            skLineSegment(sketch, "E159.11.0.18", {"start": v(107.7, -30) * mm, "end": v(108.85, -28) * mm});
            skCircle(sketch, "E159.11.0.19", {"center": v(110, -10) * mm, "radius": 1.25 * mm, "construction": true});
            skLineSegment(sketch, "E159.11.0.20", {"start": v(109.13, -21.5) * mm, "end": v(108.27, -20) * mm});
            skLineSegment(sketch, "E159.11.0.21", {"start": v(110.87, -18.5) * mm, "end": v(111.73, -20) * mm});
            skCircle(sketch, "E159.11.0.22", {"center": v(110, -20) * mm, "radius": 1.5 * mm, "construction": true});
            skLineSegment(sketch, "E159.11.0.23", {"start": v(110.72, -8.75) * mm, "end": v(111.44, -10) * mm});
            skPoint(sketch, "E159.12.0.0", {"position": v(120, -8.75) * mm});
            skLineSegment(sketch, "E159.12.0.1", {"start": v(120.72, -11.25) * mm, "end": v(119.28, -11.25) * mm});
            skLineSegment(sketch, "E159.12.0.2", {"start": v(120.87, -21.5) * mm, "end": v(119.13, -21.5) * mm});
            skLineSegment(sketch, "E159.12.0.3", {"start": v(119.13, -18.5) * mm, "end": v(120.87, -18.5) * mm});
            skLineSegment(sketch, "E159.12.0.4", {"start": v(118.56, -10) * mm, "end": v(119.28, -8.75) * mm});
            skLineSegment(sketch, "E159.12.0.5", {"start": v(121.15, -32) * mm, "end": v(118.85, -32) * mm});
            skPoint(sketch, "E159.12.0.6", {"position": v(120, -18.5) * mm});
            skLineSegment(sketch, "E159.12.0.7", {"start": v(118.85, -28) * mm, "end": v(121.15, -28) * mm});
            skPoint(sketch, "E159.12.0.8", {"position": v(120, -28) * mm});
            skLineSegment(sketch, "E159.12.0.9", {"start": v(119.28, -11.25) * mm, "end": v(118.56, -10) * mm});
            skLineSegment(sketch, "E159.12.0.10", {"start": v(119.28, -8.75) * mm, "end": v(120.72, -8.75) * mm});
            skLineSegment(sketch, "E159.12.0.11", {"start": v(118.85, -32) * mm, "end": v(117.7, -30) * mm});
            skLineSegment(sketch, "E159.12.0.12", {"start": v(121.44, -10) * mm, "end": v(120.72, -11.25) * mm});
            skLineSegment(sketch, "E159.12.0.13", {"start": v(122.3, -30) * mm, "end": v(121.15, -32) * mm});
            skLineSegment(sketch, "E159.12.0.14", {"start": v(121.15, -28) * mm, "end": v(122.3, -30) * mm});
            skCircle(sketch, "E159.12.0.15", {"center": v(120, -30) * mm, "radius": 2 * mm, "construction": true});
            skLineSegment(sketch, "E159.12.0.16", {"start": v(121.73, -20) * mm, "end": v(120.87, -21.5) * mm});
            skLineSegment(sketch, "E159.12.0.17", {"start": v(118.27, -20) * mm, "end": v(119.13, -18.5) * mm});
            skLineSegment(sketch, "E159.12.0.18", {"start": v(117.7, -30) * mm, "end": v(118.85, -28) * mm});
            skCircle(sketch, "E159.12.0.19", {"center": v(120, -10) * mm, "radius": 1.25 * mm, "construction": true});
            skLineSegment(sketch, "E159.12.0.20", {"start": v(119.13, -21.5) * mm, "end": v(118.27, -20) * mm});
            skLineSegment(sketch, "E159.12.0.21", {"start": v(120.87, -18.5) * mm, "end": v(121.73, -20) * mm});
            skCircle(sketch, "E159.12.0.22", {"center": v(120, -20) * mm, "radius": 1.5 * mm, "construction": true});
            skLineSegment(sketch, "E159.12.0.23", {"start": v(120.72, -8.75) * mm, "end": v(121.44, -10) * mm});
            skPoint(sketch, "E159.13.0.0", {"position": v(130, -8.75) * mm});
            skLineSegment(sketch, "E159.13.0.1", {"start": v(130.72, -11.25) * mm, "end": v(129.28, -11.25) * mm});
            skLineSegment(sketch, "E159.13.0.2", {"start": v(130.87, -21.5) * mm, "end": v(129.13, -21.5) * mm});
            skLineSegment(sketch, "E159.13.0.3", {"start": v(129.13, -18.5) * mm, "end": v(130.87, -18.5) * mm});
            skLineSegment(sketch, "E159.13.0.4", {"start": v(128.56, -10) * mm, "end": v(129.28, -8.75) * mm});
            skLineSegment(sketch, "E159.13.0.5", {"start": v(131.15, -32) * mm, "end": v(128.85, -32) * mm});
            skPoint(sketch, "E159.13.0.6", {"position": v(130, -18.5) * mm});
            skLineSegment(sketch, "E159.13.0.7", {"start": v(128.85, -28) * mm, "end": v(131.15, -28) * mm});
            skPoint(sketch, "E159.13.0.8", {"position": v(130, -28) * mm});
            skLineSegment(sketch, "E159.13.0.9", {"start": v(129.28, -11.25) * mm, "end": v(128.56, -10) * mm});
            skLineSegment(sketch, "E159.13.0.10", {"start": v(129.28, -8.75) * mm, "end": v(130.72, -8.75) * mm});
            skLineSegment(sketch, "E159.13.0.11", {"start": v(128.85, -32) * mm, "end": v(127.7, -30) * mm});
            skLineSegment(sketch, "E159.13.0.12", {"start": v(131.44, -10) * mm, "end": v(130.72, -11.25) * mm});
            skLineSegment(sketch, "E159.13.0.13", {"start": v(132.3, -30) * mm, "end": v(131.15, -32) * mm});
            skLineSegment(sketch, "E159.13.0.14", {"start": v(131.15, -28) * mm, "end": v(132.3, -30) * mm});
            skCircle(sketch, "E159.13.0.15", {"center": v(130, -30) * mm, "radius": 2 * mm, "construction": true});
            skLineSegment(sketch, "E159.13.0.16", {"start": v(131.73, -20) * mm, "end": v(130.87, -21.5) * mm});
            skLineSegment(sketch, "E159.13.0.17", {"start": v(128.27, -20) * mm, "end": v(129.13, -18.5) * mm});
            skLineSegment(sketch, "E159.13.0.18", {"start": v(127.7, -30) * mm, "end": v(128.85, -28) * mm});
            skCircle(sketch, "E159.13.0.19", {"center": v(130, -10) * mm, "radius": 1.25 * mm, "construction": true});
            skLineSegment(sketch, "E159.13.0.20", {"start": v(129.13, -21.5) * mm, "end": v(128.27, -20) * mm});
            skLineSegment(sketch, "E159.13.0.21", {"start": v(130.87, -18.5) * mm, "end": v(131.73, -20) * mm});
            skCircle(sketch, "E159.13.0.22", {"center": v(130, -20) * mm, "radius": 1.5 * mm, "construction": true});
            skLineSegment(sketch, "E159.13.0.23", {"start": v(130.72, -8.75) * mm, "end": v(131.44, -10) * mm});
            skLineSegment(sketch, "E159.direction1", {"start": v(0, -8.75) * mm, "end": v(10, -8.75) * mm, "construction": true});
            skPoint(sketch, "E160.0.14.0", {"position": v(140, -8.75) * mm});
            skLineSegment(sketch, "E160.1.14.0", {"start": v(140.72, -11.25) * mm, "end": v(139.28, -11.25) * mm});
            skLineSegment(sketch, "E160.4.14.0", {"start": v(140.87, -21.5) * mm, "end": v(139.13, -21.5) * mm});
            skLineSegment(sketch, "E160.7.14.0", {"start": v(139.13, -18.5) * mm, "end": v(140.87, -18.5) * mm});
            skLineSegment(sketch, "E160.10.14.0", {"start": v(138.56, -10) * mm, "end": v(139.28, -8.75) * mm});
            skLineSegment(sketch, "E160.13.14.0", {"start": v(141.15, -32) * mm, "end": v(138.85, -32) * mm});
            skPoint(sketch, "E160.16.14.0", {"position": v(140, -18.5) * mm});
            skLineSegment(sketch, "E160.17.14.0", {"start": v(138.85, -28) * mm, "end": v(141.15, -28) * mm});
            skPoint(sketch, "E160.20.14.0", {"position": v(140, -28) * mm});
            skLineSegment(sketch, "E160.21.14.0", {"start": v(139.28, -11.25) * mm, "end": v(138.56, -10) * mm});
            skLineSegment(sketch, "E160.24.14.0", {"start": v(139.28, -8.75) * mm, "end": v(140.72, -8.75) * mm});
            skLineSegment(sketch, "E160.27.14.0", {"start": v(138.85, -32) * mm, "end": v(137.7, -30) * mm});
            skLineSegment(sketch, "E160.30.14.0", {"start": v(141.44, -10) * mm, "end": v(140.72, -11.25) * mm});
            skLineSegment(sketch, "E160.33.14.0", {"start": v(142.3, -30) * mm, "end": v(141.15, -32) * mm});
            skLineSegment(sketch, "E160.36.14.0", {"start": v(141.15, -28) * mm, "end": v(142.3, -30) * mm});
            skCircle(sketch, "E160.39.14.0", {"center": v(140, -30) * mm, "radius": 2 * mm, "construction": true});
            skLineSegment(sketch, "E160.41.14.0", {"start": v(141.73, -20) * mm, "end": v(140.87, -21.5) * mm});
            skLineSegment(sketch, "E160.44.14.0", {"start": v(138.27, -20) * mm, "end": v(139.13, -18.5) * mm});
            skLineSegment(sketch, "E160.47.14.0", {"start": v(137.7, -30) * mm, "end": v(138.85, -28) * mm});
            skCircle(sketch, "E160.50.14.0", {"center": v(140, -10) * mm, "radius": 1.25 * mm, "construction": true});
            skLineSegment(sketch, "E160.52.14.0", {"start": v(139.13, -21.5) * mm, "end": v(138.27, -20) * mm});
            skLineSegment(sketch, "E160.55.14.0", {"start": v(140.87, -18.5) * mm, "end": v(141.73, -20) * mm});
            skCircle(sketch, "E160.58.14.0", {"center": v(140, -20) * mm, "radius": 1.5 * mm, "construction": true});
            skLineSegment(sketch, "E160.60.14.0", {"start": v(140.72, -8.75) * mm, "end": v(141.44, -10) * mm});
            skPoint(sketch, "E160.0.15.0", {"position": v(150, -8.75) * mm});
            skLineSegment(sketch, "E160.1.15.0", {"start": v(150.72, -11.25) * mm, "end": v(149.28, -11.25) * mm});
            skLineSegment(sketch, "E160.4.15.0", {"start": v(150.87, -21.5) * mm, "end": v(149.13, -21.5) * mm});
            skLineSegment(sketch, "E160.7.15.0", {"start": v(149.13, -18.5) * mm, "end": v(150.87, -18.5) * mm});
            skLineSegment(sketch, "E160.10.15.0", {"start": v(148.56, -10) * mm, "end": v(149.28, -8.75) * mm});
            skLineSegment(sketch, "E160.13.15.0", {"start": v(151.15, -32) * mm, "end": v(148.85, -32) * mm});
            skPoint(sketch, "E160.16.15.0", {"position": v(150, -18.5) * mm});
            skLineSegment(sketch, "E160.17.15.0", {"start": v(148.85, -28) * mm, "end": v(151.15, -28) * mm});
            skPoint(sketch, "E160.20.15.0", {"position": v(150, -28) * mm});
            skLineSegment(sketch, "E160.21.15.0", {"start": v(149.28, -11.25) * mm, "end": v(148.56, -10) * mm});
            skLineSegment(sketch, "E160.24.15.0", {"start": v(149.28, -8.75) * mm, "end": v(150.72, -8.75) * mm});
            skLineSegment(sketch, "E160.27.15.0", {"start": v(148.85, -32) * mm, "end": v(147.7, -30) * mm});
            skLineSegment(sketch, "E160.30.15.0", {"start": v(151.44, -10) * mm, "end": v(150.72, -11.25) * mm});
            skLineSegment(sketch, "E160.33.15.0", {"start": v(152.3, -30) * mm, "end": v(151.15, -32) * mm});
            skLineSegment(sketch, "E160.36.15.0", {"start": v(151.15, -28) * mm, "end": v(152.3, -30) * mm});
            skCircle(sketch, "E160.39.15.0", {"center": v(150, -30) * mm, "radius": 2 * mm, "construction": true});
            skLineSegment(sketch, "E160.41.15.0", {"start": v(151.73, -20) * mm, "end": v(150.87, -21.5) * mm});
            skLineSegment(sketch, "E160.44.15.0", {"start": v(148.27, -20) * mm, "end": v(149.13, -18.5) * mm});
            skLineSegment(sketch, "E160.47.15.0", {"start": v(147.7, -30) * mm, "end": v(148.85, -28) * mm});
            skCircle(sketch, "E160.50.15.0", {"center": v(150, -10) * mm, "radius": 1.25 * mm, "construction": true});
            skLineSegment(sketch, "E160.52.15.0", {"start": v(149.13, -21.5) * mm, "end": v(148.27, -20) * mm});
            skLineSegment(sketch, "E160.55.15.0", {"start": v(150.87, -18.5) * mm, "end": v(151.73, -20) * mm});
            skCircle(sketch, "E160.58.15.0", {"center": v(150, -20) * mm, "radius": 1.5 * mm, "construction": true});
            skLineSegment(sketch, "E160.60.15.0", {"start": v(150.72, -8.75) * mm, "end": v(151.44, -10) * mm});
            skSolve(sketch);
        }
        {
            var Q0;
            Q0 = qSketchRegion(id + "F49", true);
            extrude(context, id + "F50", {"entities" : qUnion([Q0]), "operationType" : NewBodyOperationType.REMOVE, "depth" : 10 * mm});
        }
    });
